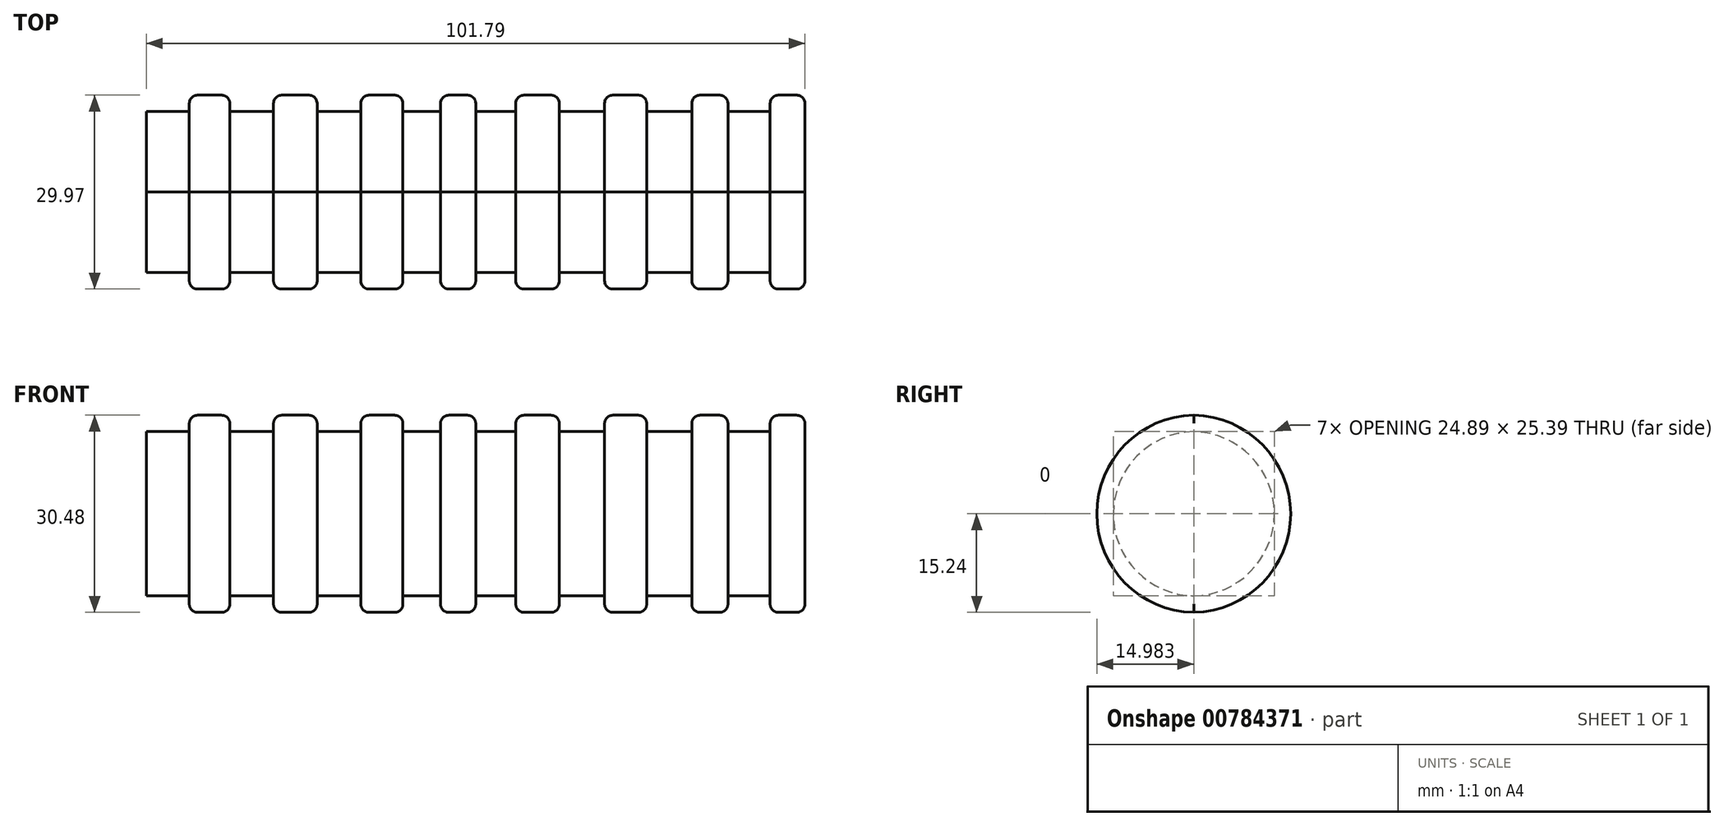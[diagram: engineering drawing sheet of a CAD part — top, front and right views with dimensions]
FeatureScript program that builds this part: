
annotation { "Feature Type Name" : "Feature", "Feature Type Description" : "" }
export const myFeature = defineFeature(function(context is Context, id is Id, definition is map)
    precondition{}
    {
        {
            var Q0;
            Q0=qCreatedBy(makeId("Top.planeOp"),FACE);
            var sketch = newSketch(context, id + "F0", { "sketchPlane" : qUnion([Q0])});
            skLineSegment(sketch, "E0.bottom", {"start": v(-61.73, 35.84) * mm, "end": v(40.06, 35.84) * mm});
            skLineSegment(sketch, "E0.top", {"start": v(-61.73, 10.95) * mm, "end": v(40.06, 10.95) * mm});
            skLineSegment(sketch, "E0.left", {"start": v(-61.73, 35.84) * mm, "end": v(-61.73, 10.95) * mm});
            skLineSegment(sketch, "E0.right", {"start": v(40.06, 35.84) * mm, "end": v(40.06, 10.95) * mm});
            skSolve(sketch);
        }
        {
            var Q0;
            Q0 = qSketchRegion(id + "F0", true);
            extrude(context, id + "F1", {"entities" : qUnion([Q0]), "depth" : 25.4 * mm, "offsetDistance" : 25.4 * mm});
        }
        {
            var Q0;
            Q0=makeQuery(id+"F1.opExtrude","CAP_FACE",FACE,{"disambiguationData":[OSD([sQuery(id+"F0.wireOp",EDGE,"E0.bottom"),sQuery(id+"F0.wireOp",EDGE,"E0.top"),sQuery(id+"F0.wireOp",EDGE,"E0.left"),sQuery(id+"F0.wireOp",EDGE,"E0.right")])],"isStart":false});
            var sketch = newSketch(context, id + "F2", { "sketchPlane" : qUnion([Q0])});
            skLineSegment(sketch, "E1.bottom", {"start": v(-55.11, 35.84) * mm, "end": v(-48.84, 35.84) * mm});
            skLineSegment(sketch, "E1.top", {"start": v(-55.11, 10.95) * mm, "end": v(-48.84, 10.95) * mm});
            skLineSegment(sketch, "E1.left", {"start": v(-55.11, 35.84) * mm, "end": v(-55.11, 10.95) * mm});
            skLineSegment(sketch, "E1.right", {"start": v(-48.84, 35.84) * mm, "end": v(-48.84, 10.95) * mm});
            skLineSegment(sketch, "E2.bottom", {"start": v(-42.09, 35.84) * mm, "end": v(-35.34, 35.84) * mm});
            skLineSegment(sketch, "E2.top", {"start": v(-42.09, 10.95) * mm, "end": v(-35.34, 10.95) * mm});
            skLineSegment(sketch, "E2.left", {"start": v(-42.09, 35.84) * mm, "end": v(-42.09, 10.95) * mm});
            skLineSegment(sketch, "E2.right", {"start": v(-35.34, 35.84) * mm, "end": v(-35.34, 10.95) * mm});
            skLineSegment(sketch, "E3.bottom", {"start": v(-28.6, 35.84) * mm, "end": v(-22.1, 35.84) * mm});
            skLineSegment(sketch, "E3.top", {"start": v(-28.6, 10.95) * mm, "end": v(-22.1, 10.95) * mm});
            skLineSegment(sketch, "E3.left", {"start": v(-28.6, 35.84) * mm, "end": v(-28.6, 10.95) * mm});
            skLineSegment(sketch, "E3.right", {"start": v(-22.1, 35.84) * mm, "end": v(-22.1, 10.95) * mm});
            skLineSegment(sketch, "E4.bottom", {"start": v(-16.27, 35.84) * mm, "end": v(-10.83, 35.84) * mm});
            skLineSegment(sketch, "E4.top", {"start": v(-16.27, 10.95) * mm, "end": v(-10.83, 10.95) * mm});
            skLineSegment(sketch, "E4.left", {"start": v(-16.27, 35.84) * mm, "end": v(-16.27, 10.95) * mm});
            skLineSegment(sketch, "E4.right", {"start": v(-10.83, 35.84) * mm, "end": v(-10.83, 10.95) * mm});
            skLineSegment(sketch, "E5.bottom", {"start": v(-4.64, 35.84) * mm, "end": v(2.1, 35.84) * mm});
            skLineSegment(sketch, "E5.top", {"start": v(-4.64, 10.95) * mm, "end": v(2.1, 10.95) * mm});
            skLineSegment(sketch, "E5.left", {"start": v(-4.64, 35.84) * mm, "end": v(-4.64, 10.95) * mm});
            skLineSegment(sketch, "E5.right", {"start": v(2.1, 35.84) * mm, "end": v(2.1, 10.95) * mm});
            skLineSegment(sketch, "E6.bottom", {"start": v(9.09, 35.84) * mm, "end": v(15.6, 35.84) * mm});
            skLineSegment(sketch, "E6.top", {"start": v(9.09, 10.95) * mm, "end": v(15.6, 10.95) * mm});
            skLineSegment(sketch, "E6.left", {"start": v(9.09, 35.84) * mm, "end": v(9.09, 10.95) * mm});
            skLineSegment(sketch, "E6.right", {"start": v(15.6, 35.84) * mm, "end": v(15.6, 10.95) * mm});
            skLineSegment(sketch, "E7.bottom", {"start": v(22.57, 35.84) * mm, "end": v(28.15, 35.84) * mm});
            skLineSegment(sketch, "E7.top", {"start": v(22.57, 10.95) * mm, "end": v(28.15, 10.95) * mm});
            skLineSegment(sketch, "E7.left", {"start": v(22.57, 35.84) * mm, "end": v(22.57, 10.95) * mm});
            skLineSegment(sketch, "E7.right", {"start": v(28.15, 35.84) * mm, "end": v(28.15, 10.95) * mm});
            skLineSegment(sketch, "E8.bottom", {"start": v(34.68, 35.84) * mm, "end": v(40.06, 35.84) * mm});
            skLineSegment(sketch, "E8.top", {"start": v(34.68, 10.95) * mm, "end": v(40.06, 10.95) * mm});
            skLineSegment(sketch, "E8.left", {"start": v(34.68, 35.84) * mm, "end": v(34.68, 10.95) * mm});
            skLineSegment(sketch, "E8.right", {"start": v(40.06, 35.84) * mm, "end": v(40.06, 10.95) * mm});
            skSolve(sketch);
        }
        {
            var Q0;
            Q0=makeQuery(id+"F2.imprint","IMPRINT",FACE,{"disambiguationData":[TD([[makeQuery(id+"F2.imprint","IMPRINT",EDGE,{"derivedFrom":sQuery(id+"F2.wireOp",EDGE,"E1.bottom")}),-1.0]])]});
            var Q1;
            Q1=makeQuery(id+"F2.imprint","IMPRINT",FACE,{"disambiguationData":[TD([[makeQuery(id+"F2.imprint","IMPRINT",EDGE,{"derivedFrom":sQuery(id+"F2.wireOp",EDGE,"E2.bottom")}),-1.0]])]});
            var Q2;
            Q2=makeQuery(id+"F2.imprint","IMPRINT",FACE,{"disambiguationData":[TD([[makeQuery(id+"F2.imprint","IMPRINT",EDGE,{"derivedFrom":sQuery(id+"F2.wireOp",EDGE,"E3.bottom")}),-1.0]])]});
            var Q3;
            Q3=makeQuery(id+"F2.imprint","IMPRINT",FACE,{"disambiguationData":[TD([[makeQuery(id+"F2.imprint","IMPRINT",EDGE,{"derivedFrom":sQuery(id+"F2.wireOp",EDGE,"E4.bottom")}),-1.0]])]});
            var Q4;
            Q4=makeQuery(id+"F2.imprint","IMPRINT",FACE,{"disambiguationData":[TD([[makeQuery(id+"F2.imprint","IMPRINT",EDGE,{"derivedFrom":sQuery(id+"F2.wireOp",EDGE,"E5.bottom")}),-1.0]])]});
            var Q5;
            Q5=makeQuery(id+"F2.imprint","IMPRINT",FACE,{"disambiguationData":[TD([[makeQuery(id+"F2.imprint","IMPRINT",EDGE,{"derivedFrom":sQuery(id+"F2.wireOp",EDGE,"E6.bottom")}),-1.0]])]});
            var Q6;
            Q6=makeQuery(id+"F2.imprint","IMPRINT",FACE,{"disambiguationData":[TD([[makeQuery(id+"F2.imprint","IMPRINT",EDGE,{"derivedFrom":sQuery(id+"F2.wireOp",EDGE,"E7.bottom")}),-1.0]])]});
            var Q7;
            Q7=makeQuery(id+"F2.imprint","IMPRINT",FACE,{"disambiguationData":[TD([[makeQuery(id+"F2.imprint","IMPRINT",EDGE,{"derivedFrom":sQuery(id+"F2.wireOp",EDGE,"E8.bottom")}),-1.0]])]});
            extrude(context, id + "F3", {"entities" : qUnion([Q0, Q1, Q2, Q3, Q4, Q5, Q6, Q7]), "operationType" : NewBodyOperationType.ADD, "depth" : 2.54 * mm, "offsetDistance" : 25.4 * mm});
        }
        {
            var Q0;
            Q0=makeQuery(id+"F3.boolean.opBoolean","MERGE",FACE,{"derivedFrom":[makeQuery(id+"F1.opExtrude","SWEPT_FACE",FACE,{"disambiguationData":[OSD([sQuery(id+"F0.wireOp",EDGE,"E0.top")])]}),makeQuery(id+"F3.opExtrude","SWEPT_FACE",FACE,{"disambiguationData":[OSD([sQuery(id+"F2.wireOp",EDGE,"E1.top")])]}),makeQuery(id+"F3.opExtrude","SWEPT_FACE",FACE,{"disambiguationData":[OSD([sQuery(id+"F2.wireOp",EDGE,"E2.top")])]}),makeQuery(id+"F3.opExtrude","SWEPT_FACE",FACE,{"disambiguationData":[OSD([sQuery(id+"F2.wireOp",EDGE,"E3.top")])]}),makeQuery(id+"F3.opExtrude","SWEPT_FACE",FACE,{"disambiguationData":[OSD([sQuery(id+"F2.wireOp",EDGE,"E4.top")])]}),makeQuery(id+"F3.opExtrude","SWEPT_FACE",FACE,{"disambiguationData":[OSD([sQuery(id+"F2.wireOp",EDGE,"E5.top")])]}),makeQuery(id+"F3.opExtrude","SWEPT_FACE",FACE,{"disambiguationData":[OSD([sQuery(id+"F2.wireOp",EDGE,"E6.top")])]}),makeQuery(id+"F3.opExtrude","SWEPT_FACE",FACE,{"disambiguationData":[OSD([sQuery(id+"F2.wireOp",EDGE,"E7.top")])]}),makeQuery(id+"F3.opExtrude","SWEPT_FACE",FACE,{"disambiguationData":[OSD([sQuery(id+"F2.wireOp",EDGE,"E8.top")])]})]});
            var sketch = newSketch(context, id + "F4", { "sketchPlane" : qUnion([Q0])});
            skLineSegment(sketch, "E9.bottom", {"start": v(-55.11, 27.94) * mm, "end": v(-48.84, 27.94) * mm});
            skLineSegment(sketch, "E9.top", {"start": v(-55.11, 0) * mm, "end": v(-48.84, 0) * mm});
            skLineSegment(sketch, "E9.left", {"start": v(-55.11, 27.94) * mm, "end": v(-55.11, 0) * mm});
            skLineSegment(sketch, "E9.right", {"start": v(-48.84, 27.94) * mm, "end": v(-48.84, 0) * mm});
            skLineSegment(sketch, "E10.bottom", {"start": v(-42.09, 27.94) * mm, "end": v(-35.34, 27.94) * mm});
            skLineSegment(sketch, "E10.top", {"start": v(-42.09, 0) * mm, "end": v(-35.34, 0) * mm});
            skLineSegment(sketch, "E10.left", {"start": v(-42.09, 27.94) * mm, "end": v(-42.09, 0) * mm});
            skLineSegment(sketch, "E10.right", {"start": v(-35.34, 27.94) * mm, "end": v(-35.34, 0) * mm});
            skLineSegment(sketch, "E11.bottom", {"start": v(-28.6, 27.94) * mm, "end": v(-22.1, 27.94) * mm});
            skLineSegment(sketch, "E11.top", {"start": v(-28.6, 0) * mm, "end": v(-22.1, 0) * mm});
            skLineSegment(sketch, "E11.left", {"start": v(-28.6, 27.94) * mm, "end": v(-28.6, 0) * mm});
            skLineSegment(sketch, "E11.right", {"start": v(-22.1, 27.94) * mm, "end": v(-22.1, 0) * mm});
            skLineSegment(sketch, "E12.bottom", {"start": v(-16.27, 27.94) * mm, "end": v(-10.83, 27.94) * mm});
            skLineSegment(sketch, "E12.top", {"start": v(-16.27, 0) * mm, "end": v(-10.83, 0) * mm});
            skLineSegment(sketch, "E12.left", {"start": v(-16.27, 27.94) * mm, "end": v(-16.27, 0) * mm});
            skLineSegment(sketch, "E12.right", {"start": v(-10.83, 27.94) * mm, "end": v(-10.83, 0) * mm});
            skLineSegment(sketch, "E13.bottom", {"start": v(-4.64, 27.94) * mm, "end": v(2.1, 27.94) * mm});
            skLineSegment(sketch, "E13.top", {"start": v(-4.64, 0) * mm, "end": v(2.1, 0) * mm});
            skLineSegment(sketch, "E13.left", {"start": v(-4.64, 27.94) * mm, "end": v(-4.64, 0) * mm});
            skLineSegment(sketch, "E13.right", {"start": v(2.1, 27.94) * mm, "end": v(2.1, 0) * mm});
            skLineSegment(sketch, "E14.bottom", {"start": v(9.09, 27.94) * mm, "end": v(15.6, 27.94) * mm});
            skLineSegment(sketch, "E14.top", {"start": v(9.09, 0) * mm, "end": v(15.6, 0) * mm});
            skLineSegment(sketch, "E14.left", {"start": v(9.09, 27.94) * mm, "end": v(9.09, 0) * mm});
            skLineSegment(sketch, "E14.right", {"start": v(15.6, 27.94) * mm, "end": v(15.6, 0) * mm});
            skLineSegment(sketch, "E15.bottom", {"start": v(22.57, 27.94) * mm, "end": v(28.15, 27.94) * mm});
            skLineSegment(sketch, "E15.top", {"start": v(22.57, 0) * mm, "end": v(28.15, 0) * mm});
            skLineSegment(sketch, "E15.left", {"start": v(22.57, 27.94) * mm, "end": v(22.57, 0) * mm});
            skLineSegment(sketch, "E15.right", {"start": v(28.15, 27.94) * mm, "end": v(28.15, 0) * mm});
            skLineSegment(sketch, "E16.bottom", {"start": v(34.68, 27.94) * mm, "end": v(40.06, 27.94) * mm});
            skLineSegment(sketch, "E16.top", {"start": v(34.68, 0) * mm, "end": v(40.06, 0) * mm});
            skLineSegment(sketch, "E16.left", {"start": v(34.68, 27.94) * mm, "end": v(34.68, 0) * mm});
            skLineSegment(sketch, "E16.right", {"start": v(40.06, 27.94) * mm, "end": v(40.06, 0) * mm});
            skSolve(sketch);
        }
        {
            var Q0;
            {var subQ1=sQuery(id+"F4.wireOp",EDGE,"E9.bottom");Q0=makeQuery(id+"F4.imprint","IMPRINT",FACE,{"disambiguationData":[TD([[makeQuery(id+"F4.imprint","IMPRINT",EDGE,{"derivedFrom":subQ1}),-1.0]])]});}
            var Q1;
            {var subQ1=sQuery(id+"F4.wireOp",EDGE,"E10.bottom");Q1=makeQuery(id+"F4.imprint","IMPRINT",FACE,{"disambiguationData":[TD([[makeQuery(id+"F4.imprint","IMPRINT",EDGE,{"derivedFrom":subQ1}),-1.0]])]});}
            var Q2;
            {var subQ1=sQuery(id+"F4.wireOp",EDGE,"E11.bottom");Q2=makeQuery(id+"F4.imprint","IMPRINT",FACE,{"disambiguationData":[TD([[makeQuery(id+"F4.imprint","IMPRINT",EDGE,{"derivedFrom":subQ1}),-1.0]])]});}
            var Q3;
            {var subQ1=sQuery(id+"F4.wireOp",EDGE,"E12.bottom");Q3=makeQuery(id+"F4.imprint","IMPRINT",FACE,{"disambiguationData":[TD([[makeQuery(id+"F4.imprint","IMPRINT",EDGE,{"derivedFrom":subQ1}),-1.0]])]});}
            var Q4;
            {var subQ1=sQuery(id+"F4.wireOp",EDGE,"E13.bottom");Q4=makeQuery(id+"F4.imprint","IMPRINT",FACE,{"disambiguationData":[TD([[makeQuery(id+"F4.imprint","IMPRINT",EDGE,{"derivedFrom":subQ1}),-1.0]])]});}
            var Q5;
            {var subQ1=sQuery(id+"F4.wireOp",EDGE,"E14.bottom");Q5=makeQuery(id+"F4.imprint","IMPRINT",FACE,{"disambiguationData":[TD([[makeQuery(id+"F4.imprint","IMPRINT",EDGE,{"derivedFrom":subQ1}),-1.0]])]});}
            var Q6;
            {var subQ1=sQuery(id+"F4.wireOp",EDGE,"E15.bottom");Q6=makeQuery(id+"F4.imprint","IMPRINT",FACE,{"disambiguationData":[TD([[makeQuery(id+"F4.imprint","IMPRINT",EDGE,{"derivedFrom":subQ1}),-1.0]])]});}
            var Q7;
            {var subQ1=sQuery(id+"F4.wireOp",EDGE,"E16.bottom");Q7=makeQuery(id+"F4.imprint","IMPRINT",FACE,{"disambiguationData":[TD([[makeQuery(id+"F4.imprint","IMPRINT",EDGE,{"derivedFrom":subQ1}),-1.0]])]});}
            extrude(context, id + "F5", {"entities" : qUnion([Q0, Q1, Q2, Q3, Q4, Q5, Q6, Q7]), "operationType" : NewBodyOperationType.ADD, "depth" : 2.54 * mm, "offsetDistance" : 25.4 * mm});
        }
        {
            var Q0;
            Q0=makeQuery(id+"F5.boolean.opBoolean","MERGE",FACE,{"derivedFrom":[makeQuery(id+"F1.opExtrude","CAP_FACE",FACE,{"disambiguationData":[OSD([sQuery(id+"F0.wireOp",EDGE,"E0.bottom"),sQuery(id+"F0.wireOp",EDGE,"E0.top"),sQuery(id+"F0.wireOp",EDGE,"E0.left"),sQuery(id+"F0.wireOp",EDGE,"E0.right")])],"isStart":true}),makeQuery(id+"F5.opExtrude","SWEPT_FACE",FACE,{"disambiguationData":[OSD([sQuery(id+"F4.wireOp",EDGE,"E9.top")])]}),makeQuery(id+"F5.opExtrude","SWEPT_FACE",FACE,{"disambiguationData":[OSD([sQuery(id+"F4.wireOp",EDGE,"E10.top")])]}),makeQuery(id+"F5.opExtrude","SWEPT_FACE",FACE,{"disambiguationData":[OSD([sQuery(id+"F4.wireOp",EDGE,"E11.top")])]}),makeQuery(id+"F5.opExtrude","SWEPT_FACE",FACE,{"disambiguationData":[OSD([sQuery(id+"F4.wireOp",EDGE,"E12.top")])]}),makeQuery(id+"F5.opExtrude","SWEPT_FACE",FACE,{"disambiguationData":[OSD([sQuery(id+"F4.wireOp",EDGE,"E13.top")])]}),makeQuery(id+"F5.opExtrude","SWEPT_FACE",FACE,{"disambiguationData":[OSD([sQuery(id+"F4.wireOp",EDGE,"E14.top")])]}),makeQuery(id+"F5.opExtrude","SWEPT_FACE",FACE,{"disambiguationData":[OSD([sQuery(id+"F4.wireOp",EDGE,"E15.top")])]}),makeQuery(id+"F5.opExtrude","SWEPT_FACE",FACE,{"disambiguationData":[OSD([sQuery(id+"F4.wireOp",EDGE,"E16.top")])]})]});
            var sketch = newSketch(context, id + "F6", { "sketchPlane" : qUnion([Q0])});
            skLineSegment(sketch, "E17.bottom", {"start": v(-55.11, -8.4) * mm, "end": v(-48.84, -8.4) * mm});
            skLineSegment(sketch, "E17.top", {"start": v(-55.11, -35.84) * mm, "end": v(-48.84, -35.84) * mm});
            skLineSegment(sketch, "E17.left", {"start": v(-55.11, -8.4) * mm, "end": v(-55.11, -35.84) * mm});
            skLineSegment(sketch, "E17.right", {"start": v(-48.84, -8.4) * mm, "end": v(-48.84, -35.84) * mm});
            skLineSegment(sketch, "E18.bottom", {"start": v(-42.09, -8.4) * mm, "end": v(-35.34, -8.4) * mm});
            skLineSegment(sketch, "E18.top", {"start": v(-42.09, -35.84) * mm, "end": v(-35.34, -35.84) * mm});
            skLineSegment(sketch, "E18.left", {"start": v(-42.09, -8.4) * mm, "end": v(-42.09, -35.84) * mm});
            skLineSegment(sketch, "E18.right", {"start": v(-35.34, -8.4) * mm, "end": v(-35.34, -35.84) * mm});
            skLineSegment(sketch, "E19.bottom", {"start": v(-28.6, -8.4) * mm, "end": v(-22.1, -8.4) * mm});
            skLineSegment(sketch, "E19.top", {"start": v(-28.6, -35.84) * mm, "end": v(-22.1, -35.84) * mm});
            skLineSegment(sketch, "E19.left", {"start": v(-28.6, -8.4) * mm, "end": v(-28.6, -35.84) * mm});
            skLineSegment(sketch, "E19.right", {"start": v(-22.1, -8.4) * mm, "end": v(-22.1, -35.84) * mm});
            skLineSegment(sketch, "E20.bottom", {"start": v(-16.27, -8.4) * mm, "end": v(-10.83, -8.4) * mm});
            skLineSegment(sketch, "E20.top", {"start": v(-16.27, -35.84) * mm, "end": v(-10.83, -35.84) * mm});
            skLineSegment(sketch, "E20.left", {"start": v(-16.27, -8.4) * mm, "end": v(-16.27, -35.84) * mm});
            skLineSegment(sketch, "E20.right", {"start": v(-10.83, -8.4) * mm, "end": v(-10.83, -35.84) * mm});
            skLineSegment(sketch, "E21.bottom", {"start": v(-4.64, -8.4) * mm, "end": v(2.1, -8.4) * mm});
            skLineSegment(sketch, "E21.top", {"start": v(-4.64, -35.84) * mm, "end": v(2.1, -35.84) * mm});
            skLineSegment(sketch, "E21.left", {"start": v(-4.64, -8.4) * mm, "end": v(-4.64, -35.84) * mm});
            skLineSegment(sketch, "E21.right", {"start": v(2.1, -8.4) * mm, "end": v(2.1, -35.84) * mm});
            skLineSegment(sketch, "E22.bottom", {"start": v(9.09, -8.4) * mm, "end": v(15.6, -8.4) * mm});
            skLineSegment(sketch, "E22.top", {"start": v(9.09, -35.84) * mm, "end": v(15.6, -35.84) * mm});
            skLineSegment(sketch, "E22.left", {"start": v(9.09, -8.4) * mm, "end": v(9.09, -35.84) * mm});
            skLineSegment(sketch, "E22.right", {"start": v(15.6, -8.4) * mm, "end": v(15.6, -35.84) * mm});
            skLineSegment(sketch, "E23.bottom", {"start": v(22.57, -8.4) * mm, "end": v(28.15, -8.4) * mm});
            skLineSegment(sketch, "E23.top", {"start": v(22.57, -35.84) * mm, "end": v(28.15, -35.84) * mm});
            skLineSegment(sketch, "E23.left", {"start": v(22.57, -8.4) * mm, "end": v(22.57, -35.84) * mm});
            skLineSegment(sketch, "E23.right", {"start": v(28.15, -8.4) * mm, "end": v(28.15, -35.84) * mm});
            skLineSegment(sketch, "E24.bottom", {"start": v(34.68, -8.4) * mm, "end": v(40.06, -8.4) * mm});
            skLineSegment(sketch, "E24.top", {"start": v(34.68, -35.84) * mm, "end": v(40.06, -35.84) * mm});
            skLineSegment(sketch, "E24.left", {"start": v(34.68, -8.4) * mm, "end": v(34.68, -35.84) * mm});
            skLineSegment(sketch, "E24.right", {"start": v(40.06, -8.4) * mm, "end": v(40.06, -35.84) * mm});
            skSolve(sketch);
        }
        {
            var Q0;
            {var subQ1=sQuery(id+"F6.wireOp",EDGE,"E17.bottom");Q0=makeQuery(id+"F6.imprint","IMPRINT",FACE,{"disambiguationData":[TD([[makeQuery(id+"F6.imprint","IMPRINT",EDGE,{"derivedFrom":subQ1}),-1.0]])]});}
            var Q1;
            {var subQ1=sQuery(id+"F6.wireOp",EDGE,"E18.bottom");Q1=makeQuery(id+"F6.imprint","IMPRINT",FACE,{"disambiguationData":[TD([[makeQuery(id+"F6.imprint","IMPRINT",EDGE,{"derivedFrom":subQ1}),-1.0]])]});}
            var Q2;
            {var subQ1=sQuery(id+"F6.wireOp",EDGE,"E19.bottom");Q2=makeQuery(id+"F6.imprint","IMPRINT",FACE,{"disambiguationData":[TD([[makeQuery(id+"F6.imprint","IMPRINT",EDGE,{"derivedFrom":subQ1}),-1.0]])]});}
            var Q3;
            {var subQ1=sQuery(id+"F6.wireOp",EDGE,"E20.bottom");Q3=makeQuery(id+"F6.imprint","IMPRINT",FACE,{"disambiguationData":[TD([[makeQuery(id+"F6.imprint","IMPRINT",EDGE,{"derivedFrom":subQ1}),-1.0]])]});}
            var Q4;
            {var subQ1=sQuery(id+"F6.wireOp",EDGE,"E21.bottom");Q4=makeQuery(id+"F6.imprint","IMPRINT",FACE,{"disambiguationData":[TD([[makeQuery(id+"F6.imprint","IMPRINT",EDGE,{"derivedFrom":subQ1}),-1.0]])]});}
            var Q5;
            {var subQ1=sQuery(id+"F6.wireOp",EDGE,"E22.bottom");Q5=makeQuery(id+"F6.imprint","IMPRINT",FACE,{"disambiguationData":[TD([[makeQuery(id+"F6.imprint","IMPRINT",EDGE,{"derivedFrom":subQ1}),-1.0]])]});}
            var Q6;
            {var subQ1=sQuery(id+"F6.wireOp",EDGE,"E23.bottom");Q6=makeQuery(id+"F6.imprint","IMPRINT",FACE,{"disambiguationData":[TD([[makeQuery(id+"F6.imprint","IMPRINT",EDGE,{"derivedFrom":subQ1}),-1.0]])]});}
            var Q7;
            {var subQ1=sQuery(id+"F6.wireOp",EDGE,"E24.bottom");Q7=makeQuery(id+"F6.imprint","IMPRINT",FACE,{"disambiguationData":[TD([[makeQuery(id+"F6.imprint","IMPRINT",EDGE,{"derivedFrom":subQ1}),-1.0]])]});}
            extrude(context, id + "F7", {"entities" : qUnion([Q0, Q1, Q2, Q3, Q4, Q5, Q6, Q7]), "operationType" : NewBodyOperationType.ADD, "depth" : 2.54 * mm, "offsetDistance" : 25.4 * mm});
        }
        {
            var Q0;
            Q0=makeQuery(id+"F7.boolean.opBoolean","MERGE",FACE,{"derivedFrom":[makeQuery(id+"F3.boolean.opBoolean","MERGE",FACE,{"derivedFrom":[makeQuery(id+"F1.opExtrude","SWEPT_FACE",FACE,{"disambiguationData":[OSD([sQuery(id+"F0.wireOp",EDGE,"E0.bottom")])]}),makeQuery(id+"F3.opExtrude","SWEPT_FACE",FACE,{"disambiguationData":[OSD([sQuery(id+"F2.wireOp",EDGE,"E1.bottom")])]}),makeQuery(id+"F3.opExtrude","SWEPT_FACE",FACE,{"disambiguationData":[OSD([sQuery(id+"F2.wireOp",EDGE,"E2.bottom")])]}),makeQuery(id+"F3.opExtrude","SWEPT_FACE",FACE,{"disambiguationData":[OSD([sQuery(id+"F2.wireOp",EDGE,"E3.bottom")])]}),makeQuery(id+"F3.opExtrude","SWEPT_FACE",FACE,{"disambiguationData":[OSD([sQuery(id+"F2.wireOp",EDGE,"E4.bottom")])]}),makeQuery(id+"F3.opExtrude","SWEPT_FACE",FACE,{"disambiguationData":[OSD([sQuery(id+"F2.wireOp",EDGE,"E5.bottom")])]}),makeQuery(id+"F3.opExtrude","SWEPT_FACE",FACE,{"disambiguationData":[OSD([sQuery(id+"F2.wireOp",EDGE,"E6.bottom")])]}),makeQuery(id+"F3.opExtrude","SWEPT_FACE",FACE,{"disambiguationData":[OSD([sQuery(id+"F2.wireOp",EDGE,"E7.bottom")])]}),makeQuery(id+"F3.opExtrude","SWEPT_FACE",FACE,{"disambiguationData":[OSD([sQuery(id+"F2.wireOp",EDGE,"E8.bottom")])]})]}),makeQuery(id+"F7.opExtrude","SWEPT_FACE",FACE,{"disambiguationData":[OSD([sQuery(id+"F6.wireOp",EDGE,"E17.top")])]}),makeQuery(id+"F7.opExtrude","SWEPT_FACE",FACE,{"disambiguationData":[OSD([sQuery(id+"F6.wireOp",EDGE,"E18.top")])]}),makeQuery(id+"F7.opExtrude","SWEPT_FACE",FACE,{"disambiguationData":[OSD([sQuery(id+"F6.wireOp",EDGE,"E19.top")])]}),makeQuery(id+"F7.opExtrude","SWEPT_FACE",FACE,{"disambiguationData":[OSD([sQuery(id+"F6.wireOp",EDGE,"E20.top")])]}),makeQuery(id+"F7.opExtrude","SWEPT_FACE",FACE,{"disambiguationData":[OSD([sQuery(id+"F6.wireOp",EDGE,"E21.top")])]}),makeQuery(id+"F7.opExtrude","SWEPT_FACE",FACE,{"disambiguationData":[OSD([sQuery(id+"F6.wireOp",EDGE,"E22.top")])]}),makeQuery(id+"F7.opExtrude","SWEPT_FACE",FACE,{"disambiguationData":[OSD([sQuery(id+"F6.wireOp",EDGE,"E23.top")])]}),makeQuery(id+"F7.opExtrude","SWEPT_FACE",FACE,{"disambiguationData":[OSD([sQuery(id+"F6.wireOp",EDGE,"E24.top")])]})]});
            var sketch = newSketch(context, id + "F8", { "sketchPlane" : qUnion([Q0])});
            skLineSegment(sketch, "E25.bottom", {"start": v(-40.06, 27.94) * mm, "end": v(-34.68, 27.94) * mm});
            skLineSegment(sketch, "E25.top", {"start": v(-40.06, -2.54) * mm, "end": v(-34.68, -2.54) * mm});
            skLineSegment(sketch, "E25.left", {"start": v(-40.06, 27.94) * mm, "end": v(-40.06, -2.54) * mm});
            skLineSegment(sketch, "E25.right", {"start": v(-34.68, 27.94) * mm, "end": v(-34.68, -2.54) * mm});
            skLineSegment(sketch, "E26.bottom", {"start": v(-28.15, 27.94) * mm, "end": v(-22.57, 27.94) * mm});
            skLineSegment(sketch, "E26.top", {"start": v(-28.15, -2.54) * mm, "end": v(-22.57, -2.54) * mm});
            skLineSegment(sketch, "E26.left", {"start": v(-28.15, 27.94) * mm, "end": v(-28.15, -2.54) * mm});
            skLineSegment(sketch, "E26.right", {"start": v(-22.57, 27.94) * mm, "end": v(-22.57, -2.54) * mm});
            skLineSegment(sketch, "E27.bottom", {"start": v(-15.6, 27.94) * mm, "end": v(-9.09, 27.94) * mm});
            skLineSegment(sketch, "E27.top", {"start": v(-15.6, -2.54) * mm, "end": v(-9.09, -2.54) * mm});
            skLineSegment(sketch, "E27.left", {"start": v(-15.6, 27.94) * mm, "end": v(-15.6, -2.54) * mm});
            skLineSegment(sketch, "E27.right", {"start": v(-9.09, 27.94) * mm, "end": v(-9.09, -2.54) * mm});
            skLineSegment(sketch, "E28.bottom", {"start": v(-2.1, 27.94) * mm, "end": v(4.64, 27.94) * mm});
            skLineSegment(sketch, "E28.top", {"start": v(-2.1, -2.54) * mm, "end": v(4.64, -2.54) * mm});
            skLineSegment(sketch, "E28.left", {"start": v(-2.1, 27.94) * mm, "end": v(-2.1, -2.54) * mm});
            skLineSegment(sketch, "E28.right", {"start": v(4.64, 27.94) * mm, "end": v(4.64, -2.54) * mm});
            skLineSegment(sketch, "E29.bottom", {"start": v(10.83, 27.94) * mm, "end": v(16.27, 27.94) * mm});
            skLineSegment(sketch, "E29.top", {"start": v(10.83, -2.54) * mm, "end": v(16.27, -2.54) * mm});
            skLineSegment(sketch, "E29.left", {"start": v(10.83, 27.94) * mm, "end": v(10.83, -2.54) * mm});
            skLineSegment(sketch, "E29.right", {"start": v(16.27, 27.94) * mm, "end": v(16.27, -2.54) * mm});
            skLineSegment(sketch, "E30.bottom", {"start": v(22.1, 27.94) * mm, "end": v(28.6, 27.94) * mm});
            skLineSegment(sketch, "E30.top", {"start": v(22.1, -2.54) * mm, "end": v(28.6, -2.54) * mm});
            skLineSegment(sketch, "E30.left", {"start": v(22.1, 27.94) * mm, "end": v(22.1, -2.54) * mm});
            skLineSegment(sketch, "E30.right", {"start": v(28.6, 27.94) * mm, "end": v(28.6, -2.54) * mm});
            skLineSegment(sketch, "E31.bottom", {"start": v(35.34, 27.94) * mm, "end": v(42.09, 27.94) * mm});
            skLineSegment(sketch, "E31.top", {"start": v(35.34, -2.54) * mm, "end": v(42.09, -2.54) * mm});
            skLineSegment(sketch, "E31.left", {"start": v(35.34, 27.94) * mm, "end": v(35.34, -2.54) * mm});
            skLineSegment(sketch, "E31.right", {"start": v(42.09, 27.94) * mm, "end": v(42.09, -2.54) * mm});
            skLineSegment(sketch, "E32.bottom", {"start": v(48.84, 27.94) * mm, "end": v(55.11, 27.94) * mm});
            skLineSegment(sketch, "E32.top", {"start": v(48.84, -2.54) * mm, "end": v(55.11, -2.54) * mm});
            skLineSegment(sketch, "E32.left", {"start": v(48.84, 27.94) * mm, "end": v(48.84, -2.54) * mm});
            skLineSegment(sketch, "E32.right", {"start": v(55.11, 27.94) * mm, "end": v(55.11, -2.54) * mm});
            skSolve(sketch);
        }
        {
            var Q0;
            {var subQ19=sQuery(id+"F8.wireOp",EDGE,"E25.bottom");Q0=makeQuery(id+"F8.imprint","IMPRINT",FACE,{"disambiguationData":[TD([[makeQuery(id+"F8.imprint","IMPRINT",EDGE,{"derivedFrom":subQ19}),1.0]])]});}
            var Q1;
            {var subQ1=sQuery(id+"F8.wireOp",EDGE,"E26.bottom");Q1=makeQuery(id+"F8.imprint","IMPRINT",FACE,{"disambiguationData":[TD([[makeQuery(id+"F8.imprint","IMPRINT",EDGE,{"derivedFrom":subQ1}),1.0]])]});}
            var Q2;
            {var subQ39=sQuery(id+"F8.wireOp",EDGE,"E27.bottom");Q2=makeQuery(id+"F8.imprint","IMPRINT",FACE,{"disambiguationData":[TD([[makeQuery(id+"F8.imprint","IMPRINT",EDGE,{"derivedFrom":subQ39}),1.0]])]});}
            var Q3;
            {var subQ39=sQuery(id+"F8.wireOp",EDGE,"E28.bottom");Q3=makeQuery(id+"F8.imprint","IMPRINT",FACE,{"disambiguationData":[TD([[makeQuery(id+"F8.imprint","IMPRINT",EDGE,{"derivedFrom":subQ39}),1.0]])]});}
            var Q4;
            {var subQ39=sQuery(id+"F8.wireOp",EDGE,"E29.bottom");Q4=makeQuery(id+"F8.imprint","IMPRINT",FACE,{"disambiguationData":[TD([[makeQuery(id+"F8.imprint","IMPRINT",EDGE,{"derivedFrom":subQ39}),1.0]])]});}
            var Q5;
            {var subQ39=sQuery(id+"F8.wireOp",EDGE,"E30.bottom");Q5=makeQuery(id+"F8.imprint","IMPRINT",FACE,{"disambiguationData":[TD([[makeQuery(id+"F8.imprint","IMPRINT",EDGE,{"derivedFrom":subQ39}),1.0]])]});}
            var Q6;
            {var subQ39=sQuery(id+"F8.wireOp",EDGE,"E31.bottom");Q6=makeQuery(id+"F8.imprint","IMPRINT",FACE,{"disambiguationData":[TD([[makeQuery(id+"F8.imprint","IMPRINT",EDGE,{"derivedFrom":subQ39}),1.0]])]});}
            var Q7;
            {var subQ1=sQuery(id+"F8.wireOp",EDGE,"E32.bottom");Q7=makeQuery(id+"F8.imprint","IMPRINT",FACE,{"disambiguationData":[TD([[makeQuery(id+"F8.imprint","IMPRINT",EDGE,{"derivedFrom":subQ1}),1.0]])]});}
            extrude(context, id + "F9", {"entities" : qUnion([Q0, Q1, Q2, Q3, Q4, Q5, Q6, Q7]), "operationType" : NewBodyOperationType.ADD, "depth" : 2.54 * mm, "offsetDistance" : 25.4 * mm});
        }
        {
            var Q0;
            {var subQ0=sQuery(id+"F0.wireOp",EDGE,"E0.bottom");Q0=makeQuery(id+"F7.boolean.opBoolean","SPLIT",EDGE,{"disambiguationData":[TD([makeQuery(id+"F3.opExtrude","SWEPT_FACE",FACE,{"disambiguationData":[OSD([sQuery(id+"F2.wireOp",EDGE,"E7.right")])]})])],"derivedFrom":makeQuery(id+"F1.opExtrude","CAP_EDGE",EDGE,{"disambiguationData":[OSD([subQ0])],"isStart":true})});}
            var Q1;
            {var subQ0=sQuery(id+"F0.wireOp",EDGE,"E0.bottom");Q1=makeQuery(id+"F7.boolean.opBoolean","SPLIT",EDGE,{"disambiguationData":[TD([makeQuery(id+"F3.opExtrude","SWEPT_FACE",FACE,{"disambiguationData":[OSD([sQuery(id+"F2.wireOp",EDGE,"E6.right")])]})])],"derivedFrom":makeQuery(id+"F1.opExtrude","CAP_EDGE",EDGE,{"disambiguationData":[OSD([subQ0])],"isStart":true})});}
            var Q2;
            {var subQ0=sQuery(id+"F0.wireOp",EDGE,"E0.bottom");Q2=makeQuery(id+"F7.boolean.opBoolean","SPLIT",EDGE,{"disambiguationData":[TD([makeQuery(id+"F3.opExtrude","SWEPT_FACE",FACE,{"disambiguationData":[OSD([sQuery(id+"F2.wireOp",EDGE,"E5.right")])]})])],"derivedFrom":makeQuery(id+"F1.opExtrude","CAP_EDGE",EDGE,{"disambiguationData":[OSD([subQ0])],"isStart":true})});}
            var Q3;
            {var subQ0=sQuery(id+"F0.wireOp",EDGE,"E0.bottom");Q3=makeQuery(id+"F7.boolean.opBoolean","SPLIT",EDGE,{"disambiguationData":[TD([makeQuery(id+"F3.opExtrude","SWEPT_FACE",FACE,{"disambiguationData":[OSD([sQuery(id+"F2.wireOp",EDGE,"E4.right")])]})])],"derivedFrom":makeQuery(id+"F1.opExtrude","CAP_EDGE",EDGE,{"disambiguationData":[OSD([subQ0])],"isStart":true})});}
            var Q4;
            {var subQ0=sQuery(id+"F0.wireOp",EDGE,"E0.bottom");Q4=makeQuery(id+"F7.boolean.opBoolean","SPLIT",EDGE,{"disambiguationData":[TD([makeQuery(id+"F3.opExtrude","SWEPT_FACE",FACE,{"disambiguationData":[OSD([sQuery(id+"F2.wireOp",EDGE,"E3.right")])]})])],"derivedFrom":makeQuery(id+"F1.opExtrude","CAP_EDGE",EDGE,{"disambiguationData":[OSD([subQ0])],"isStart":true})});}
            var Q5;
            {var subQ0=sQuery(id+"F0.wireOp",EDGE,"E0.bottom");Q5=makeQuery(id+"F7.boolean.opBoolean","SPLIT",EDGE,{"disambiguationData":[TD([makeQuery(id+"F3.opExtrude","SWEPT_FACE",FACE,{"disambiguationData":[OSD([sQuery(id+"F2.wireOp",EDGE,"E2.right")])]})])],"derivedFrom":makeQuery(id+"F1.opExtrude","CAP_EDGE",EDGE,{"disambiguationData":[OSD([subQ0])],"isStart":true})});}
            var Q6;
            {var subQ0=sQuery(id+"F0.wireOp",EDGE,"E0.bottom");Q6=makeQuery(id+"F7.boolean.opBoolean","SPLIT",EDGE,{"disambiguationData":[TD([makeQuery(id+"F3.opExtrude","SWEPT_FACE",FACE,{"disambiguationData":[OSD([sQuery(id+"F2.wireOp",EDGE,"E1.right")])]})])],"derivedFrom":makeQuery(id+"F1.opExtrude","CAP_EDGE",EDGE,{"disambiguationData":[OSD([subQ0])],"isStart":true})});}
            var Q7;
            {var subQ0=sQuery(id+"F0.wireOp",EDGE,"E0.left");var subQ1=sQuery(id+"F0.wireOp",EDGE,"E0.bottom");Q7=makeQuery(id+"F7.boolean.opBoolean","SPLIT",EDGE,{"disambiguationData":[TD([makeQuery(id+"F1.opExtrude","SWEPT_FACE",FACE,{"disambiguationData":[OSD([subQ0])]})])],"derivedFrom":makeQuery(id+"F1.opExtrude","CAP_EDGE",EDGE,{"disambiguationData":[OSD([subQ1])],"isStart":true})});}
            var Q8;
            {var subQ0=sQuery(id+"F0.wireOp",EDGE,"E0.top");Q8=makeQuery(id+"F5.boolean.opBoolean","SPLIT",EDGE,{"disambiguationData":[TD([makeQuery(id+"F3.opExtrude","SWEPT_FACE",FACE,{"disambiguationData":[OSD([sQuery(id+"F2.wireOp",EDGE,"E7.right")])]})])],"derivedFrom":makeQuery(id+"F1.opExtrude","CAP_EDGE",EDGE,{"disambiguationData":[OSD([subQ0])],"isStart":true})});}
            var Q9;
            {var subQ0=sQuery(id+"F0.wireOp",EDGE,"E0.top");Q9=makeQuery(id+"F5.boolean.opBoolean","SPLIT",EDGE,{"disambiguationData":[TD([makeQuery(id+"F3.opExtrude","SWEPT_FACE",FACE,{"disambiguationData":[OSD([sQuery(id+"F2.wireOp",EDGE,"E6.right")])]})])],"derivedFrom":makeQuery(id+"F1.opExtrude","CAP_EDGE",EDGE,{"disambiguationData":[OSD([subQ0])],"isStart":true})});}
            var Q10;
            {var subQ0=sQuery(id+"F0.wireOp",EDGE,"E0.top");Q10=makeQuery(id+"F5.boolean.opBoolean","SPLIT",EDGE,{"disambiguationData":[TD([makeQuery(id+"F3.opExtrude","SWEPT_FACE",FACE,{"disambiguationData":[OSD([sQuery(id+"F2.wireOp",EDGE,"E5.right")])]})])],"derivedFrom":makeQuery(id+"F1.opExtrude","CAP_EDGE",EDGE,{"disambiguationData":[OSD([subQ0])],"isStart":true})});}
            var Q11;
            {var subQ0=sQuery(id+"F0.wireOp",EDGE,"E0.top");Q11=makeQuery(id+"F5.boolean.opBoolean","SPLIT",EDGE,{"disambiguationData":[TD([makeQuery(id+"F3.opExtrude","SWEPT_FACE",FACE,{"disambiguationData":[OSD([sQuery(id+"F2.wireOp",EDGE,"E4.right")])]})])],"derivedFrom":makeQuery(id+"F1.opExtrude","CAP_EDGE",EDGE,{"disambiguationData":[OSD([subQ0])],"isStart":true})});}
            var Q12;
            {var subQ0=sQuery(id+"F0.wireOp",EDGE,"E0.top");Q12=makeQuery(id+"F5.boolean.opBoolean","SPLIT",EDGE,{"disambiguationData":[TD([makeQuery(id+"F3.opExtrude","SWEPT_FACE",FACE,{"disambiguationData":[OSD([sQuery(id+"F2.wireOp",EDGE,"E3.right")])]})])],"derivedFrom":makeQuery(id+"F1.opExtrude","CAP_EDGE",EDGE,{"disambiguationData":[OSD([subQ0])],"isStart":true})});}
            var Q13;
            {var subQ0=sQuery(id+"F0.wireOp",EDGE,"E0.top");Q13=makeQuery(id+"F5.boolean.opBoolean","SPLIT",EDGE,{"disambiguationData":[TD([makeQuery(id+"F3.opExtrude","SWEPT_FACE",FACE,{"disambiguationData":[OSD([sQuery(id+"F2.wireOp",EDGE,"E2.right")])]})])],"derivedFrom":makeQuery(id+"F1.opExtrude","CAP_EDGE",EDGE,{"disambiguationData":[OSD([subQ0])],"isStart":true})});}
            var Q14;
            {var subQ0=sQuery(id+"F0.wireOp",EDGE,"E0.top");Q14=makeQuery(id+"F5.boolean.opBoolean","SPLIT",EDGE,{"disambiguationData":[TD([makeQuery(id+"F3.opExtrude","SWEPT_FACE",FACE,{"disambiguationData":[OSD([sQuery(id+"F2.wireOp",EDGE,"E1.right")])]})])],"derivedFrom":makeQuery(id+"F1.opExtrude","CAP_EDGE",EDGE,{"disambiguationData":[OSD([subQ0])],"isStart":true})});}
            var Q15;
            {var subQ0=sQuery(id+"F0.wireOp",EDGE,"E0.left");var subQ1=sQuery(id+"F0.wireOp",EDGE,"E0.top");Q15=makeQuery(id+"F5.boolean.opBoolean","SPLIT",EDGE,{"disambiguationData":[TD([makeQuery(id+"F1.opExtrude","SWEPT_FACE",FACE,{"disambiguationData":[OSD([subQ0])]})])],"derivedFrom":makeQuery(id+"F1.opExtrude","CAP_EDGE",EDGE,{"disambiguationData":[OSD([subQ1])],"isStart":true})});}
            var Q16;
            {var subQ0=sQuery(id+"F0.wireOp",EDGE,"E0.top");Q16=makeQuery(id+"F3.boolean.opBoolean","SPLIT",EDGE,{"disambiguationData":[TD([makeQuery(id+"F3.opExtrude","SWEPT_FACE",FACE,{"disambiguationData":[OSD([sQuery(id+"F2.wireOp",EDGE,"E7.right")])]})])],"derivedFrom":makeQuery(id+"F1.opExtrude","CAP_EDGE",EDGE,{"disambiguationData":[OSD([subQ0])],"isStart":false})});}
            var Q17;
            {var subQ0=sQuery(id+"F0.wireOp",EDGE,"E0.top");Q17=makeQuery(id+"F3.boolean.opBoolean","SPLIT",EDGE,{"disambiguationData":[TD([makeQuery(id+"F3.opExtrude","SWEPT_FACE",FACE,{"disambiguationData":[OSD([sQuery(id+"F2.wireOp",EDGE,"E6.right")])]})])],"derivedFrom":makeQuery(id+"F1.opExtrude","CAP_EDGE",EDGE,{"disambiguationData":[OSD([subQ0])],"isStart":false})});}
            var Q18;
            {var subQ0=sQuery(id+"F0.wireOp",EDGE,"E0.top");Q18=makeQuery(id+"F3.boolean.opBoolean","SPLIT",EDGE,{"disambiguationData":[TD([makeQuery(id+"F3.opExtrude","SWEPT_FACE",FACE,{"disambiguationData":[OSD([sQuery(id+"F2.wireOp",EDGE,"E5.right")])]})])],"derivedFrom":makeQuery(id+"F1.opExtrude","CAP_EDGE",EDGE,{"disambiguationData":[OSD([subQ0])],"isStart":false})});}
            var Q19;
            {var subQ0=sQuery(id+"F0.wireOp",EDGE,"E0.top");Q19=makeQuery(id+"F3.boolean.opBoolean","SPLIT",EDGE,{"disambiguationData":[TD([makeQuery(id+"F3.opExtrude","SWEPT_FACE",FACE,{"disambiguationData":[OSD([sQuery(id+"F2.wireOp",EDGE,"E4.right")])]})])],"derivedFrom":makeQuery(id+"F1.opExtrude","CAP_EDGE",EDGE,{"disambiguationData":[OSD([subQ0])],"isStart":false})});}
            var Q20;
            {var subQ0=sQuery(id+"F0.wireOp",EDGE,"E0.top");Q20=makeQuery(id+"F3.boolean.opBoolean","SPLIT",EDGE,{"disambiguationData":[TD([makeQuery(id+"F3.opExtrude","SWEPT_FACE",FACE,{"disambiguationData":[OSD([sQuery(id+"F2.wireOp",EDGE,"E3.right")])]})])],"derivedFrom":makeQuery(id+"F1.opExtrude","CAP_EDGE",EDGE,{"disambiguationData":[OSD([subQ0])],"isStart":false})});}
            var Q21;
            {var subQ0=sQuery(id+"F0.wireOp",EDGE,"E0.top");Q21=makeQuery(id+"F3.boolean.opBoolean","SPLIT",EDGE,{"disambiguationData":[TD([makeQuery(id+"F3.opExtrude","SWEPT_FACE",FACE,{"disambiguationData":[OSD([sQuery(id+"F2.wireOp",EDGE,"E2.right")])]})])],"derivedFrom":makeQuery(id+"F1.opExtrude","CAP_EDGE",EDGE,{"disambiguationData":[OSD([subQ0])],"isStart":false})});}
            var Q22;
            {var subQ0=sQuery(id+"F0.wireOp",EDGE,"E0.top");Q22=makeQuery(id+"F3.boolean.opBoolean","SPLIT",EDGE,{"disambiguationData":[TD([makeQuery(id+"F3.opExtrude","SWEPT_FACE",FACE,{"disambiguationData":[OSD([sQuery(id+"F2.wireOp",EDGE,"E1.right")])]})])],"derivedFrom":makeQuery(id+"F1.opExtrude","CAP_EDGE",EDGE,{"disambiguationData":[OSD([subQ0])],"isStart":false})});}
            var Q23;
            {var subQ0=sQuery(id+"F0.wireOp",EDGE,"E0.left");var subQ1=sQuery(id+"F0.wireOp",EDGE,"E0.top");Q23=makeQuery(id+"F3.boolean.opBoolean","SPLIT",EDGE,{"disambiguationData":[TD([makeQuery(id+"F1.opExtrude","SWEPT_FACE",FACE,{"disambiguationData":[OSD([subQ0])]})])],"derivedFrom":makeQuery(id+"F1.opExtrude","CAP_EDGE",EDGE,{"disambiguationData":[OSD([subQ1])],"isStart":false})});}
            var Q24;
            {var subQ0=sQuery(id+"F0.wireOp",EDGE,"E0.bottom");Q24=makeQuery(id+"F3.boolean.opBoolean","SPLIT",EDGE,{"disambiguationData":[TD([makeQuery(id+"F3.opExtrude","SWEPT_FACE",FACE,{"disambiguationData":[OSD([sQuery(id+"F2.wireOp",EDGE,"E7.right")])]})])],"derivedFrom":makeQuery(id+"F1.opExtrude","CAP_EDGE",EDGE,{"disambiguationData":[OSD([subQ0])],"isStart":false})});}
            var Q25;
            {var subQ0=sQuery(id+"F0.wireOp",EDGE,"E0.bottom");Q25=makeQuery(id+"F3.boolean.opBoolean","SPLIT",EDGE,{"disambiguationData":[TD([makeQuery(id+"F3.opExtrude","SWEPT_FACE",FACE,{"disambiguationData":[OSD([sQuery(id+"F2.wireOp",EDGE,"E6.right")])]})])],"derivedFrom":makeQuery(id+"F1.opExtrude","CAP_EDGE",EDGE,{"disambiguationData":[OSD([subQ0])],"isStart":false})});}
            var Q26;
            {var subQ0=sQuery(id+"F0.wireOp",EDGE,"E0.bottom");Q26=makeQuery(id+"F3.boolean.opBoolean","SPLIT",EDGE,{"disambiguationData":[TD([makeQuery(id+"F3.opExtrude","SWEPT_FACE",FACE,{"disambiguationData":[OSD([sQuery(id+"F2.wireOp",EDGE,"E5.right")])]})])],"derivedFrom":makeQuery(id+"F1.opExtrude","CAP_EDGE",EDGE,{"disambiguationData":[OSD([subQ0])],"isStart":false})});}
            var Q27;
            {var subQ0=sQuery(id+"F0.wireOp",EDGE,"E0.bottom");Q27=makeQuery(id+"F3.boolean.opBoolean","SPLIT",EDGE,{"disambiguationData":[TD([makeQuery(id+"F3.opExtrude","SWEPT_FACE",FACE,{"disambiguationData":[OSD([sQuery(id+"F2.wireOp",EDGE,"E4.right")])]})])],"derivedFrom":makeQuery(id+"F1.opExtrude","CAP_EDGE",EDGE,{"disambiguationData":[OSD([subQ0])],"isStart":false})});}
            var Q28;
            {var subQ0=sQuery(id+"F0.wireOp",EDGE,"E0.bottom");Q28=makeQuery(id+"F3.boolean.opBoolean","SPLIT",EDGE,{"disambiguationData":[TD([makeQuery(id+"F3.opExtrude","SWEPT_FACE",FACE,{"disambiguationData":[OSD([sQuery(id+"F2.wireOp",EDGE,"E3.right")])]})])],"derivedFrom":makeQuery(id+"F1.opExtrude","CAP_EDGE",EDGE,{"disambiguationData":[OSD([subQ0])],"isStart":false})});}
            var Q29;
            {var subQ0=sQuery(id+"F0.wireOp",EDGE,"E0.bottom");Q29=makeQuery(id+"F3.boolean.opBoolean","SPLIT",EDGE,{"disambiguationData":[TD([makeQuery(id+"F3.opExtrude","SWEPT_FACE",FACE,{"disambiguationData":[OSD([sQuery(id+"F2.wireOp",EDGE,"E2.right")])]})])],"derivedFrom":makeQuery(id+"F1.opExtrude","CAP_EDGE",EDGE,{"disambiguationData":[OSD([subQ0])],"isStart":false})});}
            var Q30;
            {var subQ0=sQuery(id+"F0.wireOp",EDGE,"E0.bottom");Q30=makeQuery(id+"F3.boolean.opBoolean","SPLIT",EDGE,{"disambiguationData":[TD([makeQuery(id+"F3.opExtrude","SWEPT_FACE",FACE,{"disambiguationData":[OSD([sQuery(id+"F2.wireOp",EDGE,"E1.right")])]})])],"derivedFrom":makeQuery(id+"F1.opExtrude","CAP_EDGE",EDGE,{"disambiguationData":[OSD([subQ0])],"isStart":false})});}
            var Q31;
            {var subQ0=sQuery(id+"F0.wireOp",EDGE,"E0.bottom");var subQ1=sQuery(id+"F0.wireOp",EDGE,"E0.left");Q31=makeQuery(id+"F3.boolean.opBoolean","SPLIT",EDGE,{"disambiguationData":[TD([makeQuery(id+"F1.opExtrude","SWEPT_FACE",FACE,{"disambiguationData":[OSD([subQ1])]})])],"derivedFrom":makeQuery(id+"F1.opExtrude","CAP_EDGE",EDGE,{"disambiguationData":[OSD([subQ0])],"isStart":false})});}
            fillet(context, id + "F10", {"entities" : qUnion([Q0, Q1, Q2, Q3, Q4, Q5, Q6, Q7, Q8, Q9, Q10, Q11, Q12, Q13, Q14, Q15, Q16, Q17, Q18, Q19, Q20, Q21, Q22, Q23, Q24, Q25, Q26, Q27, Q28, Q29, Q30, Q31]), "radius" : 12.7 * mm, "tangentPropagation" : true, "allowEdgeOverflow" : false});
        }
        {
            var Q0;
            Q0=makeQuery(id+"F5.opExtrude","CAP_EDGE",EDGE,{"disambiguationData":[OSD([sQuery(id+"F4.wireOp",EDGE,"E9.bottom")])],"isStart":false});
            var Q1;
            Q1=makeQuery(id+"F5.opExtrude","CAP_EDGE",EDGE,{"disambiguationData":[OSD([sQuery(id+"F4.wireOp",EDGE,"E10.bottom")])],"isStart":false});
            var Q2;
            Q2=makeQuery(id+"F5.opExtrude","CAP_EDGE",EDGE,{"disambiguationData":[OSD([sQuery(id+"F4.wireOp",EDGE,"E11.bottom")])],"isStart":false});
            var Q3;
            Q3=makeQuery(id+"F5.opExtrude","CAP_EDGE",EDGE,{"disambiguationData":[OSD([sQuery(id+"F4.wireOp",EDGE,"E12.bottom")])],"isStart":false});
            var Q4;
            Q4=makeQuery(id+"F5.opExtrude","CAP_EDGE",EDGE,{"disambiguationData":[OSD([sQuery(id+"F4.wireOp",EDGE,"E13.bottom")])],"isStart":false});
            var Q5;
            Q5=makeQuery(id+"F5.opExtrude","CAP_EDGE",EDGE,{"disambiguationData":[OSD([sQuery(id+"F4.wireOp",EDGE,"E14.bottom")])],"isStart":false});
            var Q6;
            Q6=makeQuery(id+"F5.opExtrude","CAP_EDGE",EDGE,{"disambiguationData":[OSD([sQuery(id+"F4.wireOp",EDGE,"E15.bottom")])],"isStart":false});
            var Q7;
            Q7=makeQuery(id+"F5.opExtrude","CAP_EDGE",EDGE,{"disambiguationData":[OSD([sQuery(id+"F4.wireOp",EDGE,"E16.bottom")])],"isStart":false});
            var Q8;
            Q8=makeQuery(id+"F9.opExtrude","CAP_EDGE",EDGE,{"disambiguationData":[OSD([sQuery(id+"F8.wireOp",EDGE,"E32.bottom")])],"isStart":false});
            var Q9;
            Q9=makeQuery(id+"F9.opExtrude","CAP_EDGE",EDGE,{"disambiguationData":[OSD([sQuery(id+"F8.wireOp",EDGE,"E31.bottom")])],"isStart":false});
            var Q10;
            Q10=makeQuery(id+"F9.opExtrude","CAP_EDGE",EDGE,{"disambiguationData":[OSD([sQuery(id+"F8.wireOp",EDGE,"E30.bottom")])],"isStart":false});
            var Q11;
            Q11=makeQuery(id+"F9.opExtrude","CAP_EDGE",EDGE,{"disambiguationData":[OSD([sQuery(id+"F8.wireOp",EDGE,"E29.bottom")])],"isStart":false});
            var Q12;
            Q12=makeQuery(id+"F9.opExtrude","CAP_EDGE",EDGE,{"disambiguationData":[OSD([sQuery(id+"F8.wireOp",EDGE,"E28.bottom")])],"isStart":false});
            var Q13;
            Q13=makeQuery(id+"F9.opExtrude","CAP_EDGE",EDGE,{"disambiguationData":[OSD([sQuery(id+"F8.wireOp",EDGE,"E27.bottom")])],"isStart":false});
            var Q14;
            Q14=makeQuery(id+"F9.opExtrude","CAP_EDGE",EDGE,{"disambiguationData":[OSD([sQuery(id+"F8.wireOp",EDGE,"E26.bottom")])],"isStart":false});
            var Q15;
            Q15=makeQuery(id+"F9.opExtrude","CAP_EDGE",EDGE,{"disambiguationData":[OSD([sQuery(id+"F8.wireOp",EDGE,"E25.bottom")])],"isStart":false});
            var Q16;
            Q16=makeQuery(id+"F7.opExtrude","CAP_EDGE",EDGE,{"disambiguationData":[OSD([sQuery(id+"F6.wireOp",EDGE,"E17.bottom")])],"isStart":false});
            var Q17;
            Q17=makeQuery(id+"F7.opExtrude","CAP_EDGE",EDGE,{"disambiguationData":[OSD([sQuery(id+"F6.wireOp",EDGE,"E18.bottom")])],"isStart":false});
            var Q18;
            Q18=makeQuery(id+"F7.opExtrude","CAP_EDGE",EDGE,{"disambiguationData":[OSD([sQuery(id+"F6.wireOp",EDGE,"E19.bottom")])],"isStart":false});
            var Q19;
            Q19=makeQuery(id+"F7.opExtrude","CAP_EDGE",EDGE,{"disambiguationData":[OSD([sQuery(id+"F6.wireOp",EDGE,"E20.bottom")])],"isStart":false});
            var Q20;
            Q20=makeQuery(id+"F7.opExtrude","CAP_EDGE",EDGE,{"disambiguationData":[OSD([sQuery(id+"F6.wireOp",EDGE,"E21.bottom")])],"isStart":false});
            var Q21;
            Q21=makeQuery(id+"F7.opExtrude","CAP_EDGE",EDGE,{"disambiguationData":[OSD([sQuery(id+"F6.wireOp",EDGE,"E22.bottom")])],"isStart":false});
            var Q22;
            Q22=makeQuery(id+"F7.opExtrude","CAP_EDGE",EDGE,{"disambiguationData":[OSD([sQuery(id+"F6.wireOp",EDGE,"E23.bottom")])],"isStart":false});
            var Q23;
            Q23=makeQuery(id+"F7.opExtrude","CAP_EDGE",EDGE,{"disambiguationData":[OSD([sQuery(id+"F6.wireOp",EDGE,"E24.bottom")])],"isStart":false});
            var Q24;
            Q24=makeQuery(id+"F9.opExtrude","CAP_EDGE",EDGE,{"disambiguationData":[OSD([sQuery(id+"F8.wireOp",EDGE,"E32.top")])],"isStart":false});
            var Q25;
            Q25=makeQuery(id+"F9.opExtrude","CAP_EDGE",EDGE,{"disambiguationData":[OSD([sQuery(id+"F8.wireOp",EDGE,"E31.top")])],"isStart":false});
            var Q26;
            Q26=makeQuery(id+"F9.opExtrude","CAP_EDGE",EDGE,{"disambiguationData":[OSD([sQuery(id+"F8.wireOp",EDGE,"E30.top")])],"isStart":false});
            var Q27;
            Q27=makeQuery(id+"F9.opExtrude","CAP_EDGE",EDGE,{"disambiguationData":[OSD([sQuery(id+"F8.wireOp",EDGE,"E29.top")])],"isStart":false});
            var Q28;
            Q28=makeQuery(id+"F9.opExtrude","CAP_EDGE",EDGE,{"disambiguationData":[OSD([sQuery(id+"F8.wireOp",EDGE,"E28.top")])],"isStart":false});
            var Q29;
            Q29=makeQuery(id+"F9.opExtrude","CAP_EDGE",EDGE,{"disambiguationData":[OSD([sQuery(id+"F8.wireOp",EDGE,"E27.top")])],"isStart":false});
            var Q30;
            Q30=makeQuery(id+"F9.opExtrude","CAP_EDGE",EDGE,{"disambiguationData":[OSD([sQuery(id+"F8.wireOp",EDGE,"E26.top")])],"isStart":false});
            var Q31;
            Q31=makeQuery(id+"F9.opExtrude","CAP_EDGE",EDGE,{"disambiguationData":[OSD([sQuery(id+"F8.wireOp",EDGE,"E25.top")])],"isStart":false});
            fillet(context, id + "F11", {"entities" : qUnion([Q0, Q1, Q2, Q3, Q4, Q5, Q6, Q7, Q8, Q9, Q10, Q11, Q12, Q13, Q14, Q15, Q16, Q17, Q18, Q19, Q20, Q21, Q22, Q23, Q24, Q25, Q26, Q27, Q28, Q29, Q30, Q31]), "radius" : 15.24 * mm, "tangentPropagation" : true, "allowEdgeOverflow" : false});
        }
        {
            var Q0;
            Q0=makeQuery(id+"F11.opFillet","BLEND_EDGE",EDGE,{"blendedFrom":[makeQuery(id+"F5.opExtrude","CAP_EDGE",EDGE,{"disambiguationData":[OSD([sQuery(id+"F4.wireOp",EDGE,"E9.bottom")])],"isStart":false}),makeQuery(id+"F9.boolean.opBoolean","MERGE",FACE,{"derivedFrom":[makeQuery(id+"F7.boolean.opBoolean","MERGE",FACE,{"derivedFrom":[makeQuery(id+"F5.boolean.opBoolean","MERGE",FACE,{"derivedFrom":[makeQuery(id+"F3.opExtrude","SWEPT_FACE",FACE,{"disambiguationData":[OSD([sQuery(id+"F2.wireOp",EDGE,"E1.left")])]}),makeQuery(id+"F5.opExtrude","SWEPT_FACE",FACE,{"disambiguationData":[OSD([sQuery(id+"F4.wireOp",EDGE,"E9.left")])]})]}),makeQuery(id+"F7.opExtrude","SWEPT_FACE",FACE,{"disambiguationData":[OSD([sQuery(id+"F6.wireOp",EDGE,"E17.left")])]})]}),makeQuery(id+"F9.opExtrude","SWEPT_FACE",FACE,{"disambiguationData":[OSD([sQuery(id+"F8.wireOp",EDGE,"E32.right")])]})]})],"blendedInto":[makeQuery(id+"F9.boolean.opBoolean","MERGE",FACE,{"derivedFrom":[makeQuery(id+"F7.boolean.opBoolean","MERGE",FACE,{"derivedFrom":[makeQuery(id+"F5.boolean.opBoolean","MERGE",FACE,{"derivedFrom":[makeQuery(id+"F3.opExtrude","SWEPT_FACE",FACE,{"disambiguationData":[OSD([sQuery(id+"F2.wireOp",EDGE,"E1.left")])]}),makeQuery(id+"F5.opExtrude","SWEPT_FACE",FACE,{"disambiguationData":[OSD([sQuery(id+"F4.wireOp",EDGE,"E9.left")])]})]}),makeQuery(id+"F7.opExtrude","SWEPT_FACE",FACE,{"disambiguationData":[OSD([sQuery(id+"F6.wireOp",EDGE,"E17.left")])]})]}),makeQuery(id+"F9.opExtrude","SWEPT_FACE",FACE,{"disambiguationData":[OSD([sQuery(id+"F8.wireOp",EDGE,"E32.right")])]})]})]});
            var Q1;
            Q1=makeQuery(id+"F11.opFillet","BLEND_EDGE",EDGE,{"blendedFrom":[makeQuery(id+"F9.opExtrude","CAP_EDGE",EDGE,{"disambiguationData":[OSD([sQuery(id+"F8.wireOp",EDGE,"E32.bottom")])],"isStart":false}),makeQuery(id+"F9.boolean.opBoolean","MERGE",FACE,{"derivedFrom":[makeQuery(id+"F7.boolean.opBoolean","MERGE",FACE,{"derivedFrom":[makeQuery(id+"F5.boolean.opBoolean","MERGE",FACE,{"derivedFrom":[makeQuery(id+"F3.opExtrude","SWEPT_FACE",FACE,{"disambiguationData":[OSD([sQuery(id+"F2.wireOp",EDGE,"E1.left")])]}),makeQuery(id+"F5.opExtrude","SWEPT_FACE",FACE,{"disambiguationData":[OSD([sQuery(id+"F4.wireOp",EDGE,"E9.left")])]})]}),makeQuery(id+"F7.opExtrude","SWEPT_FACE",FACE,{"disambiguationData":[OSD([sQuery(id+"F6.wireOp",EDGE,"E17.left")])]})]}),makeQuery(id+"F9.opExtrude","SWEPT_FACE",FACE,{"disambiguationData":[OSD([sQuery(id+"F8.wireOp",EDGE,"E32.right")])]})]})],"blendedInto":[makeQuery(id+"F9.boolean.opBoolean","MERGE",FACE,{"derivedFrom":[makeQuery(id+"F7.boolean.opBoolean","MERGE",FACE,{"derivedFrom":[makeQuery(id+"F5.boolean.opBoolean","MERGE",FACE,{"derivedFrom":[makeQuery(id+"F3.opExtrude","SWEPT_FACE",FACE,{"disambiguationData":[OSD([sQuery(id+"F2.wireOp",EDGE,"E1.left")])]}),makeQuery(id+"F5.opExtrude","SWEPT_FACE",FACE,{"disambiguationData":[OSD([sQuery(id+"F4.wireOp",EDGE,"E9.left")])]})]}),makeQuery(id+"F7.opExtrude","SWEPT_FACE",FACE,{"disambiguationData":[OSD([sQuery(id+"F6.wireOp",EDGE,"E17.left")])]})]}),makeQuery(id+"F9.opExtrude","SWEPT_FACE",FACE,{"disambiguationData":[OSD([sQuery(id+"F8.wireOp",EDGE,"E32.right")])]})]})]});
            var Q2;
            Q2=makeQuery(id+"F11.opFillet","BLEND_EDGE",EDGE,{"blendedFrom":[makeQuery(id+"F5.opExtrude","CAP_EDGE",EDGE,{"disambiguationData":[OSD([sQuery(id+"F4.wireOp",EDGE,"E9.bottom")])],"isStart":false}),makeQuery(id+"F9.boolean.opBoolean","MERGE",FACE,{"derivedFrom":[makeQuery(id+"F7.boolean.opBoolean","MERGE",FACE,{"derivedFrom":[makeQuery(id+"F5.boolean.opBoolean","MERGE",FACE,{"derivedFrom":[makeQuery(id+"F3.opExtrude","SWEPT_FACE",FACE,{"disambiguationData":[OSD([sQuery(id+"F2.wireOp",EDGE,"E1.right")])]}),makeQuery(id+"F5.opExtrude","SWEPT_FACE",FACE,{"disambiguationData":[OSD([sQuery(id+"F4.wireOp",EDGE,"E9.right")])]})]}),makeQuery(id+"F7.opExtrude","SWEPT_FACE",FACE,{"disambiguationData":[OSD([sQuery(id+"F6.wireOp",EDGE,"E17.right")])]})]}),makeQuery(id+"F9.opExtrude","SWEPT_FACE",FACE,{"disambiguationData":[OSD([sQuery(id+"F8.wireOp",EDGE,"E32.left")])]})]})],"blendedInto":[makeQuery(id+"F9.boolean.opBoolean","MERGE",FACE,{"derivedFrom":[makeQuery(id+"F7.boolean.opBoolean","MERGE",FACE,{"derivedFrom":[makeQuery(id+"F5.boolean.opBoolean","MERGE",FACE,{"derivedFrom":[makeQuery(id+"F3.opExtrude","SWEPT_FACE",FACE,{"disambiguationData":[OSD([sQuery(id+"F2.wireOp",EDGE,"E1.right")])]}),makeQuery(id+"F5.opExtrude","SWEPT_FACE",FACE,{"disambiguationData":[OSD([sQuery(id+"F4.wireOp",EDGE,"E9.right")])]})]}),makeQuery(id+"F7.opExtrude","SWEPT_FACE",FACE,{"disambiguationData":[OSD([sQuery(id+"F6.wireOp",EDGE,"E17.right")])]})]}),makeQuery(id+"F9.opExtrude","SWEPT_FACE",FACE,{"disambiguationData":[OSD([sQuery(id+"F8.wireOp",EDGE,"E32.left")])]})]})]});
            var Q3;
            Q3=makeQuery(id+"F11.opFillet","BLEND_EDGE",EDGE,{"blendedFrom":[makeQuery(id+"F9.opExtrude","CAP_EDGE",EDGE,{"disambiguationData":[OSD([sQuery(id+"F8.wireOp",EDGE,"E32.bottom")])],"isStart":false}),makeQuery(id+"F9.boolean.opBoolean","MERGE",FACE,{"derivedFrom":[makeQuery(id+"F7.boolean.opBoolean","MERGE",FACE,{"derivedFrom":[makeQuery(id+"F5.boolean.opBoolean","MERGE",FACE,{"derivedFrom":[makeQuery(id+"F3.opExtrude","SWEPT_FACE",FACE,{"disambiguationData":[OSD([sQuery(id+"F2.wireOp",EDGE,"E1.right")])]}),makeQuery(id+"F5.opExtrude","SWEPT_FACE",FACE,{"disambiguationData":[OSD([sQuery(id+"F4.wireOp",EDGE,"E9.right")])]})]}),makeQuery(id+"F7.opExtrude","SWEPT_FACE",FACE,{"disambiguationData":[OSD([sQuery(id+"F6.wireOp",EDGE,"E17.right")])]})]}),makeQuery(id+"F9.opExtrude","SWEPT_FACE",FACE,{"disambiguationData":[OSD([sQuery(id+"F8.wireOp",EDGE,"E32.left")])]})]})],"blendedInto":[makeQuery(id+"F9.boolean.opBoolean","MERGE",FACE,{"derivedFrom":[makeQuery(id+"F7.boolean.opBoolean","MERGE",FACE,{"derivedFrom":[makeQuery(id+"F5.boolean.opBoolean","MERGE",FACE,{"derivedFrom":[makeQuery(id+"F3.opExtrude","SWEPT_FACE",FACE,{"disambiguationData":[OSD([sQuery(id+"F2.wireOp",EDGE,"E1.right")])]}),makeQuery(id+"F5.opExtrude","SWEPT_FACE",FACE,{"disambiguationData":[OSD([sQuery(id+"F4.wireOp",EDGE,"E9.right")])]})]}),makeQuery(id+"F7.opExtrude","SWEPT_FACE",FACE,{"disambiguationData":[OSD([sQuery(id+"F6.wireOp",EDGE,"E17.right")])]})]}),makeQuery(id+"F9.opExtrude","SWEPT_FACE",FACE,{"disambiguationData":[OSD([sQuery(id+"F8.wireOp",EDGE,"E32.left")])]})]})]});
            var Q4;
            Q4=makeQuery(id+"F11.opFillet","BLEND_EDGE",EDGE,{"blendedFrom":[makeQuery(id+"F5.opExtrude","CAP_EDGE",EDGE,{"disambiguationData":[OSD([sQuery(id+"F4.wireOp",EDGE,"E10.bottom")])],"isStart":false}),makeQuery(id+"F9.boolean.opBoolean","MERGE",FACE,{"derivedFrom":[makeQuery(id+"F7.boolean.opBoolean","MERGE",FACE,{"derivedFrom":[makeQuery(id+"F5.boolean.opBoolean","MERGE",FACE,{"derivedFrom":[makeQuery(id+"F3.opExtrude","SWEPT_FACE",FACE,{"disambiguationData":[OSD([sQuery(id+"F2.wireOp",EDGE,"E2.left")])]}),makeQuery(id+"F5.opExtrude","SWEPT_FACE",FACE,{"disambiguationData":[OSD([sQuery(id+"F4.wireOp",EDGE,"E10.left")])]})]}),makeQuery(id+"F7.opExtrude","SWEPT_FACE",FACE,{"disambiguationData":[OSD([sQuery(id+"F6.wireOp",EDGE,"E18.left")])]})]}),makeQuery(id+"F9.opExtrude","SWEPT_FACE",FACE,{"disambiguationData":[OSD([sQuery(id+"F8.wireOp",EDGE,"E31.right")])]})]})],"blendedInto":[makeQuery(id+"F9.boolean.opBoolean","MERGE",FACE,{"derivedFrom":[makeQuery(id+"F7.boolean.opBoolean","MERGE",FACE,{"derivedFrom":[makeQuery(id+"F5.boolean.opBoolean","MERGE",FACE,{"derivedFrom":[makeQuery(id+"F3.opExtrude","SWEPT_FACE",FACE,{"disambiguationData":[OSD([sQuery(id+"F2.wireOp",EDGE,"E2.left")])]}),makeQuery(id+"F5.opExtrude","SWEPT_FACE",FACE,{"disambiguationData":[OSD([sQuery(id+"F4.wireOp",EDGE,"E10.left")])]})]}),makeQuery(id+"F7.opExtrude","SWEPT_FACE",FACE,{"disambiguationData":[OSD([sQuery(id+"F6.wireOp",EDGE,"E18.left")])]})]}),makeQuery(id+"F9.opExtrude","SWEPT_FACE",FACE,{"disambiguationData":[OSD([sQuery(id+"F8.wireOp",EDGE,"E31.right")])]})]})]});
            var Q5;
            Q5=makeQuery(id+"F11.opFillet","BLEND_EDGE",EDGE,{"blendedFrom":[makeQuery(id+"F5.opExtrude","CAP_EDGE",EDGE,{"disambiguationData":[OSD([sQuery(id+"F4.wireOp",EDGE,"E10.bottom")])],"isStart":false}),makeQuery(id+"F9.boolean.opBoolean","MERGE",FACE,{"derivedFrom":[makeQuery(id+"F7.boolean.opBoolean","MERGE",FACE,{"derivedFrom":[makeQuery(id+"F5.boolean.opBoolean","MERGE",FACE,{"derivedFrom":[makeQuery(id+"F3.opExtrude","SWEPT_FACE",FACE,{"disambiguationData":[OSD([sQuery(id+"F2.wireOp",EDGE,"E2.right")])]}),makeQuery(id+"F5.opExtrude","SWEPT_FACE",FACE,{"disambiguationData":[OSD([sQuery(id+"F4.wireOp",EDGE,"E10.right")])]})]}),makeQuery(id+"F7.opExtrude","SWEPT_FACE",FACE,{"disambiguationData":[OSD([sQuery(id+"F6.wireOp",EDGE,"E18.right")])]})]}),makeQuery(id+"F9.opExtrude","SWEPT_FACE",FACE,{"disambiguationData":[OSD([sQuery(id+"F8.wireOp",EDGE,"E31.left")])]})]})],"blendedInto":[makeQuery(id+"F9.boolean.opBoolean","MERGE",FACE,{"derivedFrom":[makeQuery(id+"F7.boolean.opBoolean","MERGE",FACE,{"derivedFrom":[makeQuery(id+"F5.boolean.opBoolean","MERGE",FACE,{"derivedFrom":[makeQuery(id+"F3.opExtrude","SWEPT_FACE",FACE,{"disambiguationData":[OSD([sQuery(id+"F2.wireOp",EDGE,"E2.right")])]}),makeQuery(id+"F5.opExtrude","SWEPT_FACE",FACE,{"disambiguationData":[OSD([sQuery(id+"F4.wireOp",EDGE,"E10.right")])]})]}),makeQuery(id+"F7.opExtrude","SWEPT_FACE",FACE,{"disambiguationData":[OSD([sQuery(id+"F6.wireOp",EDGE,"E18.right")])]})]}),makeQuery(id+"F9.opExtrude","SWEPT_FACE",FACE,{"disambiguationData":[OSD([sQuery(id+"F8.wireOp",EDGE,"E31.left")])]})]})]});
            var Q6;
            Q6=makeQuery(id+"F11.opFillet","BLEND_EDGE",EDGE,{"blendedFrom":[makeQuery(id+"F9.opExtrude","CAP_EDGE",EDGE,{"disambiguationData":[OSD([sQuery(id+"F8.wireOp",EDGE,"E31.bottom")])],"isStart":false}),makeQuery(id+"F9.boolean.opBoolean","MERGE",FACE,{"derivedFrom":[makeQuery(id+"F7.boolean.opBoolean","MERGE",FACE,{"derivedFrom":[makeQuery(id+"F5.boolean.opBoolean","MERGE",FACE,{"derivedFrom":[makeQuery(id+"F3.opExtrude","SWEPT_FACE",FACE,{"disambiguationData":[OSD([sQuery(id+"F2.wireOp",EDGE,"E2.left")])]}),makeQuery(id+"F5.opExtrude","SWEPT_FACE",FACE,{"disambiguationData":[OSD([sQuery(id+"F4.wireOp",EDGE,"E10.left")])]})]}),makeQuery(id+"F7.opExtrude","SWEPT_FACE",FACE,{"disambiguationData":[OSD([sQuery(id+"F6.wireOp",EDGE,"E18.left")])]})]}),makeQuery(id+"F9.opExtrude","SWEPT_FACE",FACE,{"disambiguationData":[OSD([sQuery(id+"F8.wireOp",EDGE,"E31.right")])]})]})],"blendedInto":[makeQuery(id+"F9.boolean.opBoolean","MERGE",FACE,{"derivedFrom":[makeQuery(id+"F7.boolean.opBoolean","MERGE",FACE,{"derivedFrom":[makeQuery(id+"F5.boolean.opBoolean","MERGE",FACE,{"derivedFrom":[makeQuery(id+"F3.opExtrude","SWEPT_FACE",FACE,{"disambiguationData":[OSD([sQuery(id+"F2.wireOp",EDGE,"E2.left")])]}),makeQuery(id+"F5.opExtrude","SWEPT_FACE",FACE,{"disambiguationData":[OSD([sQuery(id+"F4.wireOp",EDGE,"E10.left")])]})]}),makeQuery(id+"F7.opExtrude","SWEPT_FACE",FACE,{"disambiguationData":[OSD([sQuery(id+"F6.wireOp",EDGE,"E18.left")])]})]}),makeQuery(id+"F9.opExtrude","SWEPT_FACE",FACE,{"disambiguationData":[OSD([sQuery(id+"F8.wireOp",EDGE,"E31.right")])]})]})]});
            var Q7;
            Q7=makeQuery(id+"F11.opFillet","BLEND_EDGE",EDGE,{"blendedFrom":[makeQuery(id+"F9.opExtrude","CAP_EDGE",EDGE,{"disambiguationData":[OSD([sQuery(id+"F8.wireOp",EDGE,"E31.bottom")])],"isStart":false}),makeQuery(id+"F9.boolean.opBoolean","MERGE",FACE,{"derivedFrom":[makeQuery(id+"F7.boolean.opBoolean","MERGE",FACE,{"derivedFrom":[makeQuery(id+"F5.boolean.opBoolean","MERGE",FACE,{"derivedFrom":[makeQuery(id+"F3.opExtrude","SWEPT_FACE",FACE,{"disambiguationData":[OSD([sQuery(id+"F2.wireOp",EDGE,"E2.right")])]}),makeQuery(id+"F5.opExtrude","SWEPT_FACE",FACE,{"disambiguationData":[OSD([sQuery(id+"F4.wireOp",EDGE,"E10.right")])]})]}),makeQuery(id+"F7.opExtrude","SWEPT_FACE",FACE,{"disambiguationData":[OSD([sQuery(id+"F6.wireOp",EDGE,"E18.right")])]})]}),makeQuery(id+"F9.opExtrude","SWEPT_FACE",FACE,{"disambiguationData":[OSD([sQuery(id+"F8.wireOp",EDGE,"E31.left")])]})]})],"blendedInto":[makeQuery(id+"F9.boolean.opBoolean","MERGE",FACE,{"derivedFrom":[makeQuery(id+"F7.boolean.opBoolean","MERGE",FACE,{"derivedFrom":[makeQuery(id+"F5.boolean.opBoolean","MERGE",FACE,{"derivedFrom":[makeQuery(id+"F3.opExtrude","SWEPT_FACE",FACE,{"disambiguationData":[OSD([sQuery(id+"F2.wireOp",EDGE,"E2.right")])]}),makeQuery(id+"F5.opExtrude","SWEPT_FACE",FACE,{"disambiguationData":[OSD([sQuery(id+"F4.wireOp",EDGE,"E10.right")])]})]}),makeQuery(id+"F7.opExtrude","SWEPT_FACE",FACE,{"disambiguationData":[OSD([sQuery(id+"F6.wireOp",EDGE,"E18.right")])]})]}),makeQuery(id+"F9.opExtrude","SWEPT_FACE",FACE,{"disambiguationData":[OSD([sQuery(id+"F8.wireOp",EDGE,"E31.left")])]})]})]});
            var Q8;
            Q8=makeQuery(id+"F11.opFillet","BLEND_EDGE",EDGE,{"blendedFrom":[makeQuery(id+"F5.opExtrude","CAP_EDGE",EDGE,{"disambiguationData":[OSD([sQuery(id+"F4.wireOp",EDGE,"E11.bottom")])],"isStart":false}),makeQuery(id+"F9.boolean.opBoolean","MERGE",FACE,{"derivedFrom":[makeQuery(id+"F7.boolean.opBoolean","MERGE",FACE,{"derivedFrom":[makeQuery(id+"F5.boolean.opBoolean","MERGE",FACE,{"derivedFrom":[makeQuery(id+"F3.opExtrude","SWEPT_FACE",FACE,{"disambiguationData":[OSD([sQuery(id+"F2.wireOp",EDGE,"E3.left")])]}),makeQuery(id+"F5.opExtrude","SWEPT_FACE",FACE,{"disambiguationData":[OSD([sQuery(id+"F4.wireOp",EDGE,"E11.left")])]})]}),makeQuery(id+"F7.opExtrude","SWEPT_FACE",FACE,{"disambiguationData":[OSD([sQuery(id+"F6.wireOp",EDGE,"E19.left")])]})]}),makeQuery(id+"F9.opExtrude","SWEPT_FACE",FACE,{"disambiguationData":[OSD([sQuery(id+"F8.wireOp",EDGE,"E30.right")])]})]})],"blendedInto":[makeQuery(id+"F9.boolean.opBoolean","MERGE",FACE,{"derivedFrom":[makeQuery(id+"F7.boolean.opBoolean","MERGE",FACE,{"derivedFrom":[makeQuery(id+"F5.boolean.opBoolean","MERGE",FACE,{"derivedFrom":[makeQuery(id+"F3.opExtrude","SWEPT_FACE",FACE,{"disambiguationData":[OSD([sQuery(id+"F2.wireOp",EDGE,"E3.left")])]}),makeQuery(id+"F5.opExtrude","SWEPT_FACE",FACE,{"disambiguationData":[OSD([sQuery(id+"F4.wireOp",EDGE,"E11.left")])]})]}),makeQuery(id+"F7.opExtrude","SWEPT_FACE",FACE,{"disambiguationData":[OSD([sQuery(id+"F6.wireOp",EDGE,"E19.left")])]})]}),makeQuery(id+"F9.opExtrude","SWEPT_FACE",FACE,{"disambiguationData":[OSD([sQuery(id+"F8.wireOp",EDGE,"E30.right")])]})]})]});
            var Q9;
            Q9=makeQuery(id+"F11.opFillet","BLEND_EDGE",EDGE,{"blendedFrom":[makeQuery(id+"F5.opExtrude","CAP_EDGE",EDGE,{"disambiguationData":[OSD([sQuery(id+"F4.wireOp",EDGE,"E11.bottom")])],"isStart":false}),makeQuery(id+"F9.boolean.opBoolean","MERGE",FACE,{"derivedFrom":[makeQuery(id+"F7.boolean.opBoolean","MERGE",FACE,{"derivedFrom":[makeQuery(id+"F5.boolean.opBoolean","MERGE",FACE,{"derivedFrom":[makeQuery(id+"F3.opExtrude","SWEPT_FACE",FACE,{"disambiguationData":[OSD([sQuery(id+"F2.wireOp",EDGE,"E3.right")])]}),makeQuery(id+"F5.opExtrude","SWEPT_FACE",FACE,{"disambiguationData":[OSD([sQuery(id+"F4.wireOp",EDGE,"E11.right")])]})]}),makeQuery(id+"F7.opExtrude","SWEPT_FACE",FACE,{"disambiguationData":[OSD([sQuery(id+"F6.wireOp",EDGE,"E19.right")])]})]}),makeQuery(id+"F9.opExtrude","SWEPT_FACE",FACE,{"disambiguationData":[OSD([sQuery(id+"F8.wireOp",EDGE,"E30.left")])]})]})],"blendedInto":[makeQuery(id+"F9.boolean.opBoolean","MERGE",FACE,{"derivedFrom":[makeQuery(id+"F7.boolean.opBoolean","MERGE",FACE,{"derivedFrom":[makeQuery(id+"F5.boolean.opBoolean","MERGE",FACE,{"derivedFrom":[makeQuery(id+"F3.opExtrude","SWEPT_FACE",FACE,{"disambiguationData":[OSD([sQuery(id+"F2.wireOp",EDGE,"E3.right")])]}),makeQuery(id+"F5.opExtrude","SWEPT_FACE",FACE,{"disambiguationData":[OSD([sQuery(id+"F4.wireOp",EDGE,"E11.right")])]})]}),makeQuery(id+"F7.opExtrude","SWEPT_FACE",FACE,{"disambiguationData":[OSD([sQuery(id+"F6.wireOp",EDGE,"E19.right")])]})]}),makeQuery(id+"F9.opExtrude","SWEPT_FACE",FACE,{"disambiguationData":[OSD([sQuery(id+"F8.wireOp",EDGE,"E30.left")])]})]})]});
            var Q10;
            Q10=makeQuery(id+"F11.opFillet","BLEND_EDGE",EDGE,{"blendedFrom":[makeQuery(id+"F9.opExtrude","CAP_EDGE",EDGE,{"disambiguationData":[OSD([sQuery(id+"F8.wireOp",EDGE,"E30.bottom")])],"isStart":false}),makeQuery(id+"F9.boolean.opBoolean","MERGE",FACE,{"derivedFrom":[makeQuery(id+"F7.boolean.opBoolean","MERGE",FACE,{"derivedFrom":[makeQuery(id+"F5.boolean.opBoolean","MERGE",FACE,{"derivedFrom":[makeQuery(id+"F3.opExtrude","SWEPT_FACE",FACE,{"disambiguationData":[OSD([sQuery(id+"F2.wireOp",EDGE,"E3.right")])]}),makeQuery(id+"F5.opExtrude","SWEPT_FACE",FACE,{"disambiguationData":[OSD([sQuery(id+"F4.wireOp",EDGE,"E11.right")])]})]}),makeQuery(id+"F7.opExtrude","SWEPT_FACE",FACE,{"disambiguationData":[OSD([sQuery(id+"F6.wireOp",EDGE,"E19.right")])]})]}),makeQuery(id+"F9.opExtrude","SWEPT_FACE",FACE,{"disambiguationData":[OSD([sQuery(id+"F8.wireOp",EDGE,"E30.left")])]})]})],"blendedInto":[makeQuery(id+"F9.boolean.opBoolean","MERGE",FACE,{"derivedFrom":[makeQuery(id+"F7.boolean.opBoolean","MERGE",FACE,{"derivedFrom":[makeQuery(id+"F5.boolean.opBoolean","MERGE",FACE,{"derivedFrom":[makeQuery(id+"F3.opExtrude","SWEPT_FACE",FACE,{"disambiguationData":[OSD([sQuery(id+"F2.wireOp",EDGE,"E3.right")])]}),makeQuery(id+"F5.opExtrude","SWEPT_FACE",FACE,{"disambiguationData":[OSD([sQuery(id+"F4.wireOp",EDGE,"E11.right")])]})]}),makeQuery(id+"F7.opExtrude","SWEPT_FACE",FACE,{"disambiguationData":[OSD([sQuery(id+"F6.wireOp",EDGE,"E19.right")])]})]}),makeQuery(id+"F9.opExtrude","SWEPT_FACE",FACE,{"disambiguationData":[OSD([sQuery(id+"F8.wireOp",EDGE,"E30.left")])]})]})]});
            var Q11;
            Q11=makeQuery(id+"F11.opFillet","BLEND_EDGE",EDGE,{"blendedFrom":[makeQuery(id+"F9.opExtrude","CAP_EDGE",EDGE,{"disambiguationData":[OSD([sQuery(id+"F8.wireOp",EDGE,"E30.bottom")])],"isStart":false}),makeQuery(id+"F9.boolean.opBoolean","MERGE",FACE,{"derivedFrom":[makeQuery(id+"F7.boolean.opBoolean","MERGE",FACE,{"derivedFrom":[makeQuery(id+"F5.boolean.opBoolean","MERGE",FACE,{"derivedFrom":[makeQuery(id+"F3.opExtrude","SWEPT_FACE",FACE,{"disambiguationData":[OSD([sQuery(id+"F2.wireOp",EDGE,"E3.left")])]}),makeQuery(id+"F5.opExtrude","SWEPT_FACE",FACE,{"disambiguationData":[OSD([sQuery(id+"F4.wireOp",EDGE,"E11.left")])]})]}),makeQuery(id+"F7.opExtrude","SWEPT_FACE",FACE,{"disambiguationData":[OSD([sQuery(id+"F6.wireOp",EDGE,"E19.left")])]})]}),makeQuery(id+"F9.opExtrude","SWEPT_FACE",FACE,{"disambiguationData":[OSD([sQuery(id+"F8.wireOp",EDGE,"E30.right")])]})]})],"blendedInto":[makeQuery(id+"F9.boolean.opBoolean","MERGE",FACE,{"derivedFrom":[makeQuery(id+"F7.boolean.opBoolean","MERGE",FACE,{"derivedFrom":[makeQuery(id+"F5.boolean.opBoolean","MERGE",FACE,{"derivedFrom":[makeQuery(id+"F3.opExtrude","SWEPT_FACE",FACE,{"disambiguationData":[OSD([sQuery(id+"F2.wireOp",EDGE,"E3.left")])]}),makeQuery(id+"F5.opExtrude","SWEPT_FACE",FACE,{"disambiguationData":[OSD([sQuery(id+"F4.wireOp",EDGE,"E11.left")])]})]}),makeQuery(id+"F7.opExtrude","SWEPT_FACE",FACE,{"disambiguationData":[OSD([sQuery(id+"F6.wireOp",EDGE,"E19.left")])]})]}),makeQuery(id+"F9.opExtrude","SWEPT_FACE",FACE,{"disambiguationData":[OSD([sQuery(id+"F8.wireOp",EDGE,"E30.right")])]})]})]});
            var Q12;
            Q12=makeQuery(id+"F11.opFillet","BLEND_EDGE",EDGE,{"blendedFrom":[makeQuery(id+"F5.opExtrude","CAP_EDGE",EDGE,{"disambiguationData":[OSD([sQuery(id+"F4.wireOp",EDGE,"E12.bottom")])],"isStart":false}),makeQuery(id+"F9.boolean.opBoolean","MERGE",FACE,{"derivedFrom":[makeQuery(id+"F7.boolean.opBoolean","MERGE",FACE,{"derivedFrom":[makeQuery(id+"F5.boolean.opBoolean","MERGE",FACE,{"derivedFrom":[makeQuery(id+"F3.opExtrude","SWEPT_FACE",FACE,{"disambiguationData":[OSD([sQuery(id+"F2.wireOp",EDGE,"E4.left")])]}),makeQuery(id+"F5.opExtrude","SWEPT_FACE",FACE,{"disambiguationData":[OSD([sQuery(id+"F4.wireOp",EDGE,"E12.left")])]})]}),makeQuery(id+"F7.opExtrude","SWEPT_FACE",FACE,{"disambiguationData":[OSD([sQuery(id+"F6.wireOp",EDGE,"E20.left")])]})]}),makeQuery(id+"F9.opExtrude","SWEPT_FACE",FACE,{"disambiguationData":[OSD([sQuery(id+"F8.wireOp",EDGE,"E29.right")])]})]})],"blendedInto":[makeQuery(id+"F9.boolean.opBoolean","MERGE",FACE,{"derivedFrom":[makeQuery(id+"F7.boolean.opBoolean","MERGE",FACE,{"derivedFrom":[makeQuery(id+"F5.boolean.opBoolean","MERGE",FACE,{"derivedFrom":[makeQuery(id+"F3.opExtrude","SWEPT_FACE",FACE,{"disambiguationData":[OSD([sQuery(id+"F2.wireOp",EDGE,"E4.left")])]}),makeQuery(id+"F5.opExtrude","SWEPT_FACE",FACE,{"disambiguationData":[OSD([sQuery(id+"F4.wireOp",EDGE,"E12.left")])]})]}),makeQuery(id+"F7.opExtrude","SWEPT_FACE",FACE,{"disambiguationData":[OSD([sQuery(id+"F6.wireOp",EDGE,"E20.left")])]})]}),makeQuery(id+"F9.opExtrude","SWEPT_FACE",FACE,{"disambiguationData":[OSD([sQuery(id+"F8.wireOp",EDGE,"E29.right")])]})]})]});
            var Q13;
            Q13=makeQuery(id+"F11.opFillet","BLEND_EDGE",EDGE,{"blendedFrom":[makeQuery(id+"F9.opExtrude","CAP_EDGE",EDGE,{"disambiguationData":[OSD([sQuery(id+"F8.wireOp",EDGE,"E29.bottom")])],"isStart":false}),makeQuery(id+"F9.boolean.opBoolean","MERGE",FACE,{"derivedFrom":[makeQuery(id+"F7.boolean.opBoolean","MERGE",FACE,{"derivedFrom":[makeQuery(id+"F5.boolean.opBoolean","MERGE",FACE,{"derivedFrom":[makeQuery(id+"F3.opExtrude","SWEPT_FACE",FACE,{"disambiguationData":[OSD([sQuery(id+"F2.wireOp",EDGE,"E4.left")])]}),makeQuery(id+"F5.opExtrude","SWEPT_FACE",FACE,{"disambiguationData":[OSD([sQuery(id+"F4.wireOp",EDGE,"E12.left")])]})]}),makeQuery(id+"F7.opExtrude","SWEPT_FACE",FACE,{"disambiguationData":[OSD([sQuery(id+"F6.wireOp",EDGE,"E20.left")])]})]}),makeQuery(id+"F9.opExtrude","SWEPT_FACE",FACE,{"disambiguationData":[OSD([sQuery(id+"F8.wireOp",EDGE,"E29.right")])]})]})],"blendedInto":[makeQuery(id+"F9.boolean.opBoolean","MERGE",FACE,{"derivedFrom":[makeQuery(id+"F7.boolean.opBoolean","MERGE",FACE,{"derivedFrom":[makeQuery(id+"F5.boolean.opBoolean","MERGE",FACE,{"derivedFrom":[makeQuery(id+"F3.opExtrude","SWEPT_FACE",FACE,{"disambiguationData":[OSD([sQuery(id+"F2.wireOp",EDGE,"E4.left")])]}),makeQuery(id+"F5.opExtrude","SWEPT_FACE",FACE,{"disambiguationData":[OSD([sQuery(id+"F4.wireOp",EDGE,"E12.left")])]})]}),makeQuery(id+"F7.opExtrude","SWEPT_FACE",FACE,{"disambiguationData":[OSD([sQuery(id+"F6.wireOp",EDGE,"E20.left")])]})]}),makeQuery(id+"F9.opExtrude","SWEPT_FACE",FACE,{"disambiguationData":[OSD([sQuery(id+"F8.wireOp",EDGE,"E29.right")])]})]})]});
            var Q14;
            Q14=makeQuery(id+"F11.opFillet","BLEND_EDGE",EDGE,{"blendedFrom":[makeQuery(id+"F5.opExtrude","CAP_EDGE",EDGE,{"disambiguationData":[OSD([sQuery(id+"F4.wireOp",EDGE,"E12.bottom")])],"isStart":false}),makeQuery(id+"F9.boolean.opBoolean","MERGE",FACE,{"derivedFrom":[makeQuery(id+"F7.boolean.opBoolean","MERGE",FACE,{"derivedFrom":[makeQuery(id+"F5.boolean.opBoolean","MERGE",FACE,{"derivedFrom":[makeQuery(id+"F3.opExtrude","SWEPT_FACE",FACE,{"disambiguationData":[OSD([sQuery(id+"F2.wireOp",EDGE,"E4.right")])]}),makeQuery(id+"F5.opExtrude","SWEPT_FACE",FACE,{"disambiguationData":[OSD([sQuery(id+"F4.wireOp",EDGE,"E12.right")])]})]}),makeQuery(id+"F7.opExtrude","SWEPT_FACE",FACE,{"disambiguationData":[OSD([sQuery(id+"F6.wireOp",EDGE,"E20.right")])]})]}),makeQuery(id+"F9.opExtrude","SWEPT_FACE",FACE,{"disambiguationData":[OSD([sQuery(id+"F8.wireOp",EDGE,"E29.left")])]})]})],"blendedInto":[makeQuery(id+"F9.boolean.opBoolean","MERGE",FACE,{"derivedFrom":[makeQuery(id+"F7.boolean.opBoolean","MERGE",FACE,{"derivedFrom":[makeQuery(id+"F5.boolean.opBoolean","MERGE",FACE,{"derivedFrom":[makeQuery(id+"F3.opExtrude","SWEPT_FACE",FACE,{"disambiguationData":[OSD([sQuery(id+"F2.wireOp",EDGE,"E4.right")])]}),makeQuery(id+"F5.opExtrude","SWEPT_FACE",FACE,{"disambiguationData":[OSD([sQuery(id+"F4.wireOp",EDGE,"E12.right")])]})]}),makeQuery(id+"F7.opExtrude","SWEPT_FACE",FACE,{"disambiguationData":[OSD([sQuery(id+"F6.wireOp",EDGE,"E20.right")])]})]}),makeQuery(id+"F9.opExtrude","SWEPT_FACE",FACE,{"disambiguationData":[OSD([sQuery(id+"F8.wireOp",EDGE,"E29.left")])]})]})]});
            var Q15;
            Q15=makeQuery(id+"F11.opFillet","BLEND_EDGE",EDGE,{"blendedFrom":[makeQuery(id+"F9.opExtrude","CAP_EDGE",EDGE,{"disambiguationData":[OSD([sQuery(id+"F8.wireOp",EDGE,"E29.bottom")])],"isStart":false}),makeQuery(id+"F9.boolean.opBoolean","MERGE",FACE,{"derivedFrom":[makeQuery(id+"F7.boolean.opBoolean","MERGE",FACE,{"derivedFrom":[makeQuery(id+"F5.boolean.opBoolean","MERGE",FACE,{"derivedFrom":[makeQuery(id+"F3.opExtrude","SWEPT_FACE",FACE,{"disambiguationData":[OSD([sQuery(id+"F2.wireOp",EDGE,"E4.right")])]}),makeQuery(id+"F5.opExtrude","SWEPT_FACE",FACE,{"disambiguationData":[OSD([sQuery(id+"F4.wireOp",EDGE,"E12.right")])]})]}),makeQuery(id+"F7.opExtrude","SWEPT_FACE",FACE,{"disambiguationData":[OSD([sQuery(id+"F6.wireOp",EDGE,"E20.right")])]})]}),makeQuery(id+"F9.opExtrude","SWEPT_FACE",FACE,{"disambiguationData":[OSD([sQuery(id+"F8.wireOp",EDGE,"E29.left")])]})]})],"blendedInto":[makeQuery(id+"F9.boolean.opBoolean","MERGE",FACE,{"derivedFrom":[makeQuery(id+"F7.boolean.opBoolean","MERGE",FACE,{"derivedFrom":[makeQuery(id+"F5.boolean.opBoolean","MERGE",FACE,{"derivedFrom":[makeQuery(id+"F3.opExtrude","SWEPT_FACE",FACE,{"disambiguationData":[OSD([sQuery(id+"F2.wireOp",EDGE,"E4.right")])]}),makeQuery(id+"F5.opExtrude","SWEPT_FACE",FACE,{"disambiguationData":[OSD([sQuery(id+"F4.wireOp",EDGE,"E12.right")])]})]}),makeQuery(id+"F7.opExtrude","SWEPT_FACE",FACE,{"disambiguationData":[OSD([sQuery(id+"F6.wireOp",EDGE,"E20.right")])]})]}),makeQuery(id+"F9.opExtrude","SWEPT_FACE",FACE,{"disambiguationData":[OSD([sQuery(id+"F8.wireOp",EDGE,"E29.left")])]})]})]});
            var Q16;
            Q16=makeQuery(id+"F11.opFillet","BLEND_EDGE",EDGE,{"blendedFrom":[makeQuery(id+"F5.opExtrude","CAP_EDGE",EDGE,{"disambiguationData":[OSD([sQuery(id+"F4.wireOp",EDGE,"E13.bottom")])],"isStart":false}),makeQuery(id+"F9.boolean.opBoolean","MERGE",FACE,{"derivedFrom":[makeQuery(id+"F7.boolean.opBoolean","MERGE",FACE,{"derivedFrom":[makeQuery(id+"F5.boolean.opBoolean","MERGE",FACE,{"derivedFrom":[makeQuery(id+"F3.opExtrude","SWEPT_FACE",FACE,{"disambiguationData":[OSD([sQuery(id+"F2.wireOp",EDGE,"E5.left")])]}),makeQuery(id+"F5.opExtrude","SWEPT_FACE",FACE,{"disambiguationData":[OSD([sQuery(id+"F4.wireOp",EDGE,"E13.left")])]})]}),makeQuery(id+"F7.opExtrude","SWEPT_FACE",FACE,{"disambiguationData":[OSD([sQuery(id+"F6.wireOp",EDGE,"E21.left")])]})]}),makeQuery(id+"F9.opExtrude","SWEPT_FACE",FACE,{"disambiguationData":[OSD([sQuery(id+"F8.wireOp",EDGE,"E28.right")])]})]})],"blendedInto":[makeQuery(id+"F9.boolean.opBoolean","MERGE",FACE,{"derivedFrom":[makeQuery(id+"F7.boolean.opBoolean","MERGE",FACE,{"derivedFrom":[makeQuery(id+"F5.boolean.opBoolean","MERGE",FACE,{"derivedFrom":[makeQuery(id+"F3.opExtrude","SWEPT_FACE",FACE,{"disambiguationData":[OSD([sQuery(id+"F2.wireOp",EDGE,"E5.left")])]}),makeQuery(id+"F5.opExtrude","SWEPT_FACE",FACE,{"disambiguationData":[OSD([sQuery(id+"F4.wireOp",EDGE,"E13.left")])]})]}),makeQuery(id+"F7.opExtrude","SWEPT_FACE",FACE,{"disambiguationData":[OSD([sQuery(id+"F6.wireOp",EDGE,"E21.left")])]})]}),makeQuery(id+"F9.opExtrude","SWEPT_FACE",FACE,{"disambiguationData":[OSD([sQuery(id+"F8.wireOp",EDGE,"E28.right")])]})]})]});
            var Q17;
            Q17=makeQuery(id+"F11.opFillet","BLEND_EDGE",EDGE,{"blendedFrom":[makeQuery(id+"F9.opExtrude","CAP_EDGE",EDGE,{"disambiguationData":[OSD([sQuery(id+"F8.wireOp",EDGE,"E28.bottom")])],"isStart":false}),makeQuery(id+"F9.boolean.opBoolean","MERGE",FACE,{"derivedFrom":[makeQuery(id+"F7.boolean.opBoolean","MERGE",FACE,{"derivedFrom":[makeQuery(id+"F5.boolean.opBoolean","MERGE",FACE,{"derivedFrom":[makeQuery(id+"F3.opExtrude","SWEPT_FACE",FACE,{"disambiguationData":[OSD([sQuery(id+"F2.wireOp",EDGE,"E5.left")])]}),makeQuery(id+"F5.opExtrude","SWEPT_FACE",FACE,{"disambiguationData":[OSD([sQuery(id+"F4.wireOp",EDGE,"E13.left")])]})]}),makeQuery(id+"F7.opExtrude","SWEPT_FACE",FACE,{"disambiguationData":[OSD([sQuery(id+"F6.wireOp",EDGE,"E21.left")])]})]}),makeQuery(id+"F9.opExtrude","SWEPT_FACE",FACE,{"disambiguationData":[OSD([sQuery(id+"F8.wireOp",EDGE,"E28.right")])]})]})],"blendedInto":[makeQuery(id+"F9.boolean.opBoolean","MERGE",FACE,{"derivedFrom":[makeQuery(id+"F7.boolean.opBoolean","MERGE",FACE,{"derivedFrom":[makeQuery(id+"F5.boolean.opBoolean","MERGE",FACE,{"derivedFrom":[makeQuery(id+"F3.opExtrude","SWEPT_FACE",FACE,{"disambiguationData":[OSD([sQuery(id+"F2.wireOp",EDGE,"E5.left")])]}),makeQuery(id+"F5.opExtrude","SWEPT_FACE",FACE,{"disambiguationData":[OSD([sQuery(id+"F4.wireOp",EDGE,"E13.left")])]})]}),makeQuery(id+"F7.opExtrude","SWEPT_FACE",FACE,{"disambiguationData":[OSD([sQuery(id+"F6.wireOp",EDGE,"E21.left")])]})]}),makeQuery(id+"F9.opExtrude","SWEPT_FACE",FACE,{"disambiguationData":[OSD([sQuery(id+"F8.wireOp",EDGE,"E28.right")])]})]})]});
            var Q18;
            Q18=makeQuery(id+"F11.opFillet","BLEND_EDGE",EDGE,{"blendedFrom":[makeQuery(id+"F5.opExtrude","CAP_EDGE",EDGE,{"disambiguationData":[OSD([sQuery(id+"F4.wireOp",EDGE,"E13.bottom")])],"isStart":false}),makeQuery(id+"F9.boolean.opBoolean","MERGE",FACE,{"derivedFrom":[makeQuery(id+"F7.boolean.opBoolean","MERGE",FACE,{"derivedFrom":[makeQuery(id+"F5.boolean.opBoolean","MERGE",FACE,{"derivedFrom":[makeQuery(id+"F3.opExtrude","SWEPT_FACE",FACE,{"disambiguationData":[OSD([sQuery(id+"F2.wireOp",EDGE,"E5.right")])]}),makeQuery(id+"F5.opExtrude","SWEPT_FACE",FACE,{"disambiguationData":[OSD([sQuery(id+"F4.wireOp",EDGE,"E13.right")])]})]}),makeQuery(id+"F7.opExtrude","SWEPT_FACE",FACE,{"disambiguationData":[OSD([sQuery(id+"F6.wireOp",EDGE,"E21.right")])]})]}),makeQuery(id+"F9.opExtrude","SWEPT_FACE",FACE,{"disambiguationData":[OSD([sQuery(id+"F8.wireOp",EDGE,"E28.left")])]})]})],"blendedInto":[makeQuery(id+"F9.boolean.opBoolean","MERGE",FACE,{"derivedFrom":[makeQuery(id+"F7.boolean.opBoolean","MERGE",FACE,{"derivedFrom":[makeQuery(id+"F5.boolean.opBoolean","MERGE",FACE,{"derivedFrom":[makeQuery(id+"F3.opExtrude","SWEPT_FACE",FACE,{"disambiguationData":[OSD([sQuery(id+"F2.wireOp",EDGE,"E5.right")])]}),makeQuery(id+"F5.opExtrude","SWEPT_FACE",FACE,{"disambiguationData":[OSD([sQuery(id+"F4.wireOp",EDGE,"E13.right")])]})]}),makeQuery(id+"F7.opExtrude","SWEPT_FACE",FACE,{"disambiguationData":[OSD([sQuery(id+"F6.wireOp",EDGE,"E21.right")])]})]}),makeQuery(id+"F9.opExtrude","SWEPT_FACE",FACE,{"disambiguationData":[OSD([sQuery(id+"F8.wireOp",EDGE,"E28.left")])]})]})]});
            var Q19;
            Q19=makeQuery(id+"F11.opFillet","BLEND_EDGE",EDGE,{"blendedFrom":[makeQuery(id+"F9.opExtrude","CAP_EDGE",EDGE,{"disambiguationData":[OSD([sQuery(id+"F8.wireOp",EDGE,"E28.bottom")])],"isStart":false}),makeQuery(id+"F9.boolean.opBoolean","MERGE",FACE,{"derivedFrom":[makeQuery(id+"F7.boolean.opBoolean","MERGE",FACE,{"derivedFrom":[makeQuery(id+"F5.boolean.opBoolean","MERGE",FACE,{"derivedFrom":[makeQuery(id+"F3.opExtrude","SWEPT_FACE",FACE,{"disambiguationData":[OSD([sQuery(id+"F2.wireOp",EDGE,"E5.right")])]}),makeQuery(id+"F5.opExtrude","SWEPT_FACE",FACE,{"disambiguationData":[OSD([sQuery(id+"F4.wireOp",EDGE,"E13.right")])]})]}),makeQuery(id+"F7.opExtrude","SWEPT_FACE",FACE,{"disambiguationData":[OSD([sQuery(id+"F6.wireOp",EDGE,"E21.right")])]})]}),makeQuery(id+"F9.opExtrude","SWEPT_FACE",FACE,{"disambiguationData":[OSD([sQuery(id+"F8.wireOp",EDGE,"E28.left")])]})]})],"blendedInto":[makeQuery(id+"F9.boolean.opBoolean","MERGE",FACE,{"derivedFrom":[makeQuery(id+"F7.boolean.opBoolean","MERGE",FACE,{"derivedFrom":[makeQuery(id+"F5.boolean.opBoolean","MERGE",FACE,{"derivedFrom":[makeQuery(id+"F3.opExtrude","SWEPT_FACE",FACE,{"disambiguationData":[OSD([sQuery(id+"F2.wireOp",EDGE,"E5.right")])]}),makeQuery(id+"F5.opExtrude","SWEPT_FACE",FACE,{"disambiguationData":[OSD([sQuery(id+"F4.wireOp",EDGE,"E13.right")])]})]}),makeQuery(id+"F7.opExtrude","SWEPT_FACE",FACE,{"disambiguationData":[OSD([sQuery(id+"F6.wireOp",EDGE,"E21.right")])]})]}),makeQuery(id+"F9.opExtrude","SWEPT_FACE",FACE,{"disambiguationData":[OSD([sQuery(id+"F8.wireOp",EDGE,"E28.left")])]})]})]});
            var Q20;
            Q20=makeQuery(id+"F11.opFillet","BLEND_EDGE",EDGE,{"blendedFrom":[makeQuery(id+"F5.opExtrude","CAP_EDGE",EDGE,{"disambiguationData":[OSD([sQuery(id+"F4.wireOp",EDGE,"E14.bottom")])],"isStart":false}),makeQuery(id+"F9.boolean.opBoolean","MERGE",FACE,{"derivedFrom":[makeQuery(id+"F7.boolean.opBoolean","MERGE",FACE,{"derivedFrom":[makeQuery(id+"F5.boolean.opBoolean","MERGE",FACE,{"derivedFrom":[makeQuery(id+"F3.opExtrude","SWEPT_FACE",FACE,{"disambiguationData":[OSD([sQuery(id+"F2.wireOp",EDGE,"E6.left")])]}),makeQuery(id+"F5.opExtrude","SWEPT_FACE",FACE,{"disambiguationData":[OSD([sQuery(id+"F4.wireOp",EDGE,"E14.left")])]})]}),makeQuery(id+"F7.opExtrude","SWEPT_FACE",FACE,{"disambiguationData":[OSD([sQuery(id+"F6.wireOp",EDGE,"E22.left")])]})]}),makeQuery(id+"F9.opExtrude","SWEPT_FACE",FACE,{"disambiguationData":[OSD([sQuery(id+"F8.wireOp",EDGE,"E27.right")])]})]})],"blendedInto":[makeQuery(id+"F9.boolean.opBoolean","MERGE",FACE,{"derivedFrom":[makeQuery(id+"F7.boolean.opBoolean","MERGE",FACE,{"derivedFrom":[makeQuery(id+"F5.boolean.opBoolean","MERGE",FACE,{"derivedFrom":[makeQuery(id+"F3.opExtrude","SWEPT_FACE",FACE,{"disambiguationData":[OSD([sQuery(id+"F2.wireOp",EDGE,"E6.left")])]}),makeQuery(id+"F5.opExtrude","SWEPT_FACE",FACE,{"disambiguationData":[OSD([sQuery(id+"F4.wireOp",EDGE,"E14.left")])]})]}),makeQuery(id+"F7.opExtrude","SWEPT_FACE",FACE,{"disambiguationData":[OSD([sQuery(id+"F6.wireOp",EDGE,"E22.left")])]})]}),makeQuery(id+"F9.opExtrude","SWEPT_FACE",FACE,{"disambiguationData":[OSD([sQuery(id+"F8.wireOp",EDGE,"E27.right")])]})]})]});
            var Q21;
            Q21=makeQuery(id+"F11.opFillet","BLEND_EDGE",EDGE,{"blendedFrom":[makeQuery(id+"F9.opExtrude","CAP_EDGE",EDGE,{"disambiguationData":[OSD([sQuery(id+"F8.wireOp",EDGE,"E27.bottom")])],"isStart":false}),makeQuery(id+"F9.boolean.opBoolean","MERGE",FACE,{"derivedFrom":[makeQuery(id+"F7.boolean.opBoolean","MERGE",FACE,{"derivedFrom":[makeQuery(id+"F5.boolean.opBoolean","MERGE",FACE,{"derivedFrom":[makeQuery(id+"F3.opExtrude","SWEPT_FACE",FACE,{"disambiguationData":[OSD([sQuery(id+"F2.wireOp",EDGE,"E6.left")])]}),makeQuery(id+"F5.opExtrude","SWEPT_FACE",FACE,{"disambiguationData":[OSD([sQuery(id+"F4.wireOp",EDGE,"E14.left")])]})]}),makeQuery(id+"F7.opExtrude","SWEPT_FACE",FACE,{"disambiguationData":[OSD([sQuery(id+"F6.wireOp",EDGE,"E22.left")])]})]}),makeQuery(id+"F9.opExtrude","SWEPT_FACE",FACE,{"disambiguationData":[OSD([sQuery(id+"F8.wireOp",EDGE,"E27.right")])]})]})],"blendedInto":[makeQuery(id+"F9.boolean.opBoolean","MERGE",FACE,{"derivedFrom":[makeQuery(id+"F7.boolean.opBoolean","MERGE",FACE,{"derivedFrom":[makeQuery(id+"F5.boolean.opBoolean","MERGE",FACE,{"derivedFrom":[makeQuery(id+"F3.opExtrude","SWEPT_FACE",FACE,{"disambiguationData":[OSD([sQuery(id+"F2.wireOp",EDGE,"E6.left")])]}),makeQuery(id+"F5.opExtrude","SWEPT_FACE",FACE,{"disambiguationData":[OSD([sQuery(id+"F4.wireOp",EDGE,"E14.left")])]})]}),makeQuery(id+"F7.opExtrude","SWEPT_FACE",FACE,{"disambiguationData":[OSD([sQuery(id+"F6.wireOp",EDGE,"E22.left")])]})]}),makeQuery(id+"F9.opExtrude","SWEPT_FACE",FACE,{"disambiguationData":[OSD([sQuery(id+"F8.wireOp",EDGE,"E27.right")])]})]})]});
            var Q22;
            Q22=makeQuery(id+"F11.opFillet","BLEND_EDGE",EDGE,{"blendedFrom":[makeQuery(id+"F5.opExtrude","CAP_EDGE",EDGE,{"disambiguationData":[OSD([sQuery(id+"F4.wireOp",EDGE,"E14.bottom")])],"isStart":false}),makeQuery(id+"F9.boolean.opBoolean","MERGE",FACE,{"derivedFrom":[makeQuery(id+"F7.boolean.opBoolean","MERGE",FACE,{"derivedFrom":[makeQuery(id+"F5.boolean.opBoolean","MERGE",FACE,{"derivedFrom":[makeQuery(id+"F3.opExtrude","SWEPT_FACE",FACE,{"disambiguationData":[OSD([sQuery(id+"F2.wireOp",EDGE,"E6.right")])]}),makeQuery(id+"F5.opExtrude","SWEPT_FACE",FACE,{"disambiguationData":[OSD([sQuery(id+"F4.wireOp",EDGE,"E14.right")])]})]}),makeQuery(id+"F7.opExtrude","SWEPT_FACE",FACE,{"disambiguationData":[OSD([sQuery(id+"F6.wireOp",EDGE,"E22.right")])]})]}),makeQuery(id+"F9.opExtrude","SWEPT_FACE",FACE,{"disambiguationData":[OSD([sQuery(id+"F8.wireOp",EDGE,"E27.left")])]})]})],"blendedInto":[makeQuery(id+"F9.boolean.opBoolean","MERGE",FACE,{"derivedFrom":[makeQuery(id+"F7.boolean.opBoolean","MERGE",FACE,{"derivedFrom":[makeQuery(id+"F5.boolean.opBoolean","MERGE",FACE,{"derivedFrom":[makeQuery(id+"F3.opExtrude","SWEPT_FACE",FACE,{"disambiguationData":[OSD([sQuery(id+"F2.wireOp",EDGE,"E6.right")])]}),makeQuery(id+"F5.opExtrude","SWEPT_FACE",FACE,{"disambiguationData":[OSD([sQuery(id+"F4.wireOp",EDGE,"E14.right")])]})]}),makeQuery(id+"F7.opExtrude","SWEPT_FACE",FACE,{"disambiguationData":[OSD([sQuery(id+"F6.wireOp",EDGE,"E22.right")])]})]}),makeQuery(id+"F9.opExtrude","SWEPT_FACE",FACE,{"disambiguationData":[OSD([sQuery(id+"F8.wireOp",EDGE,"E27.left")])]})]})]});
            var Q23;
            Q23=makeQuery(id+"F11.opFillet","BLEND_EDGE",EDGE,{"blendedFrom":[makeQuery(id+"F9.opExtrude","CAP_EDGE",EDGE,{"disambiguationData":[OSD([sQuery(id+"F8.wireOp",EDGE,"E27.bottom")])],"isStart":false}),makeQuery(id+"F9.boolean.opBoolean","MERGE",FACE,{"derivedFrom":[makeQuery(id+"F7.boolean.opBoolean","MERGE",FACE,{"derivedFrom":[makeQuery(id+"F5.boolean.opBoolean","MERGE",FACE,{"derivedFrom":[makeQuery(id+"F3.opExtrude","SWEPT_FACE",FACE,{"disambiguationData":[OSD([sQuery(id+"F2.wireOp",EDGE,"E6.right")])]}),makeQuery(id+"F5.opExtrude","SWEPT_FACE",FACE,{"disambiguationData":[OSD([sQuery(id+"F4.wireOp",EDGE,"E14.right")])]})]}),makeQuery(id+"F7.opExtrude","SWEPT_FACE",FACE,{"disambiguationData":[OSD([sQuery(id+"F6.wireOp",EDGE,"E22.right")])]})]}),makeQuery(id+"F9.opExtrude","SWEPT_FACE",FACE,{"disambiguationData":[OSD([sQuery(id+"F8.wireOp",EDGE,"E27.left")])]})]})],"blendedInto":[makeQuery(id+"F9.boolean.opBoolean","MERGE",FACE,{"derivedFrom":[makeQuery(id+"F7.boolean.opBoolean","MERGE",FACE,{"derivedFrom":[makeQuery(id+"F5.boolean.opBoolean","MERGE",FACE,{"derivedFrom":[makeQuery(id+"F3.opExtrude","SWEPT_FACE",FACE,{"disambiguationData":[OSD([sQuery(id+"F2.wireOp",EDGE,"E6.right")])]}),makeQuery(id+"F5.opExtrude","SWEPT_FACE",FACE,{"disambiguationData":[OSD([sQuery(id+"F4.wireOp",EDGE,"E14.right")])]})]}),makeQuery(id+"F7.opExtrude","SWEPT_FACE",FACE,{"disambiguationData":[OSD([sQuery(id+"F6.wireOp",EDGE,"E22.right")])]})]}),makeQuery(id+"F9.opExtrude","SWEPT_FACE",FACE,{"disambiguationData":[OSD([sQuery(id+"F8.wireOp",EDGE,"E27.left")])]})]})]});
            var Q24;
            Q24=makeQuery(id+"F11.opFillet","BLEND_EDGE",EDGE,{"blendedFrom":[makeQuery(id+"F5.opExtrude","CAP_EDGE",EDGE,{"disambiguationData":[OSD([sQuery(id+"F4.wireOp",EDGE,"E15.bottom")])],"isStart":false}),makeQuery(id+"F9.boolean.opBoolean","MERGE",FACE,{"derivedFrom":[makeQuery(id+"F7.boolean.opBoolean","MERGE",FACE,{"derivedFrom":[makeQuery(id+"F5.boolean.opBoolean","MERGE",FACE,{"derivedFrom":[makeQuery(id+"F3.opExtrude","SWEPT_FACE",FACE,{"disambiguationData":[OSD([sQuery(id+"F2.wireOp",EDGE,"E7.left")])]}),makeQuery(id+"F5.opExtrude","SWEPT_FACE",FACE,{"disambiguationData":[OSD([sQuery(id+"F4.wireOp",EDGE,"E15.left")])]})]}),makeQuery(id+"F7.opExtrude","SWEPT_FACE",FACE,{"disambiguationData":[OSD([sQuery(id+"F6.wireOp",EDGE,"E23.left")])]})]}),makeQuery(id+"F9.opExtrude","SWEPT_FACE",FACE,{"disambiguationData":[OSD([sQuery(id+"F8.wireOp",EDGE,"E26.right")])]})]})],"blendedInto":[makeQuery(id+"F9.boolean.opBoolean","MERGE",FACE,{"derivedFrom":[makeQuery(id+"F7.boolean.opBoolean","MERGE",FACE,{"derivedFrom":[makeQuery(id+"F5.boolean.opBoolean","MERGE",FACE,{"derivedFrom":[makeQuery(id+"F3.opExtrude","SWEPT_FACE",FACE,{"disambiguationData":[OSD([sQuery(id+"F2.wireOp",EDGE,"E7.left")])]}),makeQuery(id+"F5.opExtrude","SWEPT_FACE",FACE,{"disambiguationData":[OSD([sQuery(id+"F4.wireOp",EDGE,"E15.left")])]})]}),makeQuery(id+"F7.opExtrude","SWEPT_FACE",FACE,{"disambiguationData":[OSD([sQuery(id+"F6.wireOp",EDGE,"E23.left")])]})]}),makeQuery(id+"F9.opExtrude","SWEPT_FACE",FACE,{"disambiguationData":[OSD([sQuery(id+"F8.wireOp",EDGE,"E26.right")])]})]})]});
            var Q25;
            Q25=makeQuery(id+"F11.opFillet","BLEND_EDGE",EDGE,{"blendedFrom":[makeQuery(id+"F9.opExtrude","CAP_EDGE",EDGE,{"disambiguationData":[OSD([sQuery(id+"F8.wireOp",EDGE,"E26.bottom")])],"isStart":false}),makeQuery(id+"F9.boolean.opBoolean","MERGE",FACE,{"derivedFrom":[makeQuery(id+"F7.boolean.opBoolean","MERGE",FACE,{"derivedFrom":[makeQuery(id+"F5.boolean.opBoolean","MERGE",FACE,{"derivedFrom":[makeQuery(id+"F3.opExtrude","SWEPT_FACE",FACE,{"disambiguationData":[OSD([sQuery(id+"F2.wireOp",EDGE,"E7.left")])]}),makeQuery(id+"F5.opExtrude","SWEPT_FACE",FACE,{"disambiguationData":[OSD([sQuery(id+"F4.wireOp",EDGE,"E15.left")])]})]}),makeQuery(id+"F7.opExtrude","SWEPT_FACE",FACE,{"disambiguationData":[OSD([sQuery(id+"F6.wireOp",EDGE,"E23.left")])]})]}),makeQuery(id+"F9.opExtrude","SWEPT_FACE",FACE,{"disambiguationData":[OSD([sQuery(id+"F8.wireOp",EDGE,"E26.right")])]})]})],"blendedInto":[makeQuery(id+"F9.boolean.opBoolean","MERGE",FACE,{"derivedFrom":[makeQuery(id+"F7.boolean.opBoolean","MERGE",FACE,{"derivedFrom":[makeQuery(id+"F5.boolean.opBoolean","MERGE",FACE,{"derivedFrom":[makeQuery(id+"F3.opExtrude","SWEPT_FACE",FACE,{"disambiguationData":[OSD([sQuery(id+"F2.wireOp",EDGE,"E7.left")])]}),makeQuery(id+"F5.opExtrude","SWEPT_FACE",FACE,{"disambiguationData":[OSD([sQuery(id+"F4.wireOp",EDGE,"E15.left")])]})]}),makeQuery(id+"F7.opExtrude","SWEPT_FACE",FACE,{"disambiguationData":[OSD([sQuery(id+"F6.wireOp",EDGE,"E23.left")])]})]}),makeQuery(id+"F9.opExtrude","SWEPT_FACE",FACE,{"disambiguationData":[OSD([sQuery(id+"F8.wireOp",EDGE,"E26.right")])]})]})]});
            var Q26;
            Q26=makeQuery(id+"F11.opFillet","BLEND_EDGE",EDGE,{"blendedFrom":[makeQuery(id+"F5.opExtrude","CAP_EDGE",EDGE,{"disambiguationData":[OSD([sQuery(id+"F4.wireOp",EDGE,"E15.bottom")])],"isStart":false}),makeQuery(id+"F9.boolean.opBoolean","MERGE",FACE,{"derivedFrom":[makeQuery(id+"F7.boolean.opBoolean","MERGE",FACE,{"derivedFrom":[makeQuery(id+"F5.boolean.opBoolean","MERGE",FACE,{"derivedFrom":[makeQuery(id+"F3.opExtrude","SWEPT_FACE",FACE,{"disambiguationData":[OSD([sQuery(id+"F2.wireOp",EDGE,"E7.right")])]}),makeQuery(id+"F5.opExtrude","SWEPT_FACE",FACE,{"disambiguationData":[OSD([sQuery(id+"F4.wireOp",EDGE,"E15.right")])]})]}),makeQuery(id+"F7.opExtrude","SWEPT_FACE",FACE,{"disambiguationData":[OSD([sQuery(id+"F6.wireOp",EDGE,"E23.right")])]})]}),makeQuery(id+"F9.opExtrude","SWEPT_FACE",FACE,{"disambiguationData":[OSD([sQuery(id+"F8.wireOp",EDGE,"E26.left")])]})]})],"blendedInto":[makeQuery(id+"F9.boolean.opBoolean","MERGE",FACE,{"derivedFrom":[makeQuery(id+"F7.boolean.opBoolean","MERGE",FACE,{"derivedFrom":[makeQuery(id+"F5.boolean.opBoolean","MERGE",FACE,{"derivedFrom":[makeQuery(id+"F3.opExtrude","SWEPT_FACE",FACE,{"disambiguationData":[OSD([sQuery(id+"F2.wireOp",EDGE,"E7.right")])]}),makeQuery(id+"F5.opExtrude","SWEPT_FACE",FACE,{"disambiguationData":[OSD([sQuery(id+"F4.wireOp",EDGE,"E15.right")])]})]}),makeQuery(id+"F7.opExtrude","SWEPT_FACE",FACE,{"disambiguationData":[OSD([sQuery(id+"F6.wireOp",EDGE,"E23.right")])]})]}),makeQuery(id+"F9.opExtrude","SWEPT_FACE",FACE,{"disambiguationData":[OSD([sQuery(id+"F8.wireOp",EDGE,"E26.left")])]})]})]});
            var Q27;
            Q27=makeQuery(id+"F11.opFillet","BLEND_EDGE",EDGE,{"blendedFrom":[makeQuery(id+"F9.opExtrude","CAP_EDGE",EDGE,{"disambiguationData":[OSD([sQuery(id+"F8.wireOp",EDGE,"E26.bottom")])],"isStart":false}),makeQuery(id+"F9.boolean.opBoolean","MERGE",FACE,{"derivedFrom":[makeQuery(id+"F7.boolean.opBoolean","MERGE",FACE,{"derivedFrom":[makeQuery(id+"F5.boolean.opBoolean","MERGE",FACE,{"derivedFrom":[makeQuery(id+"F3.opExtrude","SWEPT_FACE",FACE,{"disambiguationData":[OSD([sQuery(id+"F2.wireOp",EDGE,"E7.right")])]}),makeQuery(id+"F5.opExtrude","SWEPT_FACE",FACE,{"disambiguationData":[OSD([sQuery(id+"F4.wireOp",EDGE,"E15.right")])]})]}),makeQuery(id+"F7.opExtrude","SWEPT_FACE",FACE,{"disambiguationData":[OSD([sQuery(id+"F6.wireOp",EDGE,"E23.right")])]})]}),makeQuery(id+"F9.opExtrude","SWEPT_FACE",FACE,{"disambiguationData":[OSD([sQuery(id+"F8.wireOp",EDGE,"E26.left")])]})]})],"blendedInto":[makeQuery(id+"F9.boolean.opBoolean","MERGE",FACE,{"derivedFrom":[makeQuery(id+"F7.boolean.opBoolean","MERGE",FACE,{"derivedFrom":[makeQuery(id+"F5.boolean.opBoolean","MERGE",FACE,{"derivedFrom":[makeQuery(id+"F3.opExtrude","SWEPT_FACE",FACE,{"disambiguationData":[OSD([sQuery(id+"F2.wireOp",EDGE,"E7.right")])]}),makeQuery(id+"F5.opExtrude","SWEPT_FACE",FACE,{"disambiguationData":[OSD([sQuery(id+"F4.wireOp",EDGE,"E15.right")])]})]}),makeQuery(id+"F7.opExtrude","SWEPT_FACE",FACE,{"disambiguationData":[OSD([sQuery(id+"F6.wireOp",EDGE,"E23.right")])]})]}),makeQuery(id+"F9.opExtrude","SWEPT_FACE",FACE,{"disambiguationData":[OSD([sQuery(id+"F8.wireOp",EDGE,"E26.left")])]})]})]});
            var Q28;
            Q28=makeQuery(id+"F11.opFillet","BLEND_EDGE",EDGE,{"blendedFrom":[makeQuery(id+"F5.opExtrude","CAP_EDGE",EDGE,{"disambiguationData":[OSD([sQuery(id+"F4.wireOp",EDGE,"E16.bottom")])],"isStart":false}),makeQuery(id+"F9.boolean.opBoolean","MERGE",FACE,{"derivedFrom":[makeQuery(id+"F7.boolean.opBoolean","MERGE",FACE,{"derivedFrom":[makeQuery(id+"F5.boolean.opBoolean","MERGE",FACE,{"derivedFrom":[makeQuery(id+"F3.opExtrude","SWEPT_FACE",FACE,{"disambiguationData":[OSD([sQuery(id+"F2.wireOp",EDGE,"E8.left")])]}),makeQuery(id+"F5.opExtrude","SWEPT_FACE",FACE,{"disambiguationData":[OSD([sQuery(id+"F4.wireOp",EDGE,"E16.left")])]})]}),makeQuery(id+"F7.opExtrude","SWEPT_FACE",FACE,{"disambiguationData":[OSD([sQuery(id+"F6.wireOp",EDGE,"E24.left")])]})]}),makeQuery(id+"F9.opExtrude","SWEPT_FACE",FACE,{"disambiguationData":[OSD([sQuery(id+"F8.wireOp",EDGE,"E25.right")])]})]})],"blendedInto":[makeQuery(id+"F9.boolean.opBoolean","MERGE",FACE,{"derivedFrom":[makeQuery(id+"F7.boolean.opBoolean","MERGE",FACE,{"derivedFrom":[makeQuery(id+"F5.boolean.opBoolean","MERGE",FACE,{"derivedFrom":[makeQuery(id+"F3.opExtrude","SWEPT_FACE",FACE,{"disambiguationData":[OSD([sQuery(id+"F2.wireOp",EDGE,"E8.left")])]}),makeQuery(id+"F5.opExtrude","SWEPT_FACE",FACE,{"disambiguationData":[OSD([sQuery(id+"F4.wireOp",EDGE,"E16.left")])]})]}),makeQuery(id+"F7.opExtrude","SWEPT_FACE",FACE,{"disambiguationData":[OSD([sQuery(id+"F6.wireOp",EDGE,"E24.left")])]})]}),makeQuery(id+"F9.opExtrude","SWEPT_FACE",FACE,{"disambiguationData":[OSD([sQuery(id+"F8.wireOp",EDGE,"E25.right")])]})]})]});
            var Q29;
            Q29=makeQuery(id+"F11.opFillet","BLEND_EDGE",EDGE,{"blendedFrom":[makeQuery(id+"F9.opExtrude","CAP_EDGE",EDGE,{"disambiguationData":[OSD([sQuery(id+"F8.wireOp",EDGE,"E25.bottom")])],"isStart":false}),makeQuery(id+"F9.boolean.opBoolean","MERGE",FACE,{"derivedFrom":[makeQuery(id+"F7.boolean.opBoolean","MERGE",FACE,{"derivedFrom":[makeQuery(id+"F5.boolean.opBoolean","MERGE",FACE,{"derivedFrom":[makeQuery(id+"F3.opExtrude","SWEPT_FACE",FACE,{"disambiguationData":[OSD([sQuery(id+"F2.wireOp",EDGE,"E8.left")])]}),makeQuery(id+"F5.opExtrude","SWEPT_FACE",FACE,{"disambiguationData":[OSD([sQuery(id+"F4.wireOp",EDGE,"E16.left")])]})]}),makeQuery(id+"F7.opExtrude","SWEPT_FACE",FACE,{"disambiguationData":[OSD([sQuery(id+"F6.wireOp",EDGE,"E24.left")])]})]}),makeQuery(id+"F9.opExtrude","SWEPT_FACE",FACE,{"disambiguationData":[OSD([sQuery(id+"F8.wireOp",EDGE,"E25.right")])]})]})],"blendedInto":[makeQuery(id+"F9.boolean.opBoolean","MERGE",FACE,{"derivedFrom":[makeQuery(id+"F7.boolean.opBoolean","MERGE",FACE,{"derivedFrom":[makeQuery(id+"F5.boolean.opBoolean","MERGE",FACE,{"derivedFrom":[makeQuery(id+"F3.opExtrude","SWEPT_FACE",FACE,{"disambiguationData":[OSD([sQuery(id+"F2.wireOp",EDGE,"E8.left")])]}),makeQuery(id+"F5.opExtrude","SWEPT_FACE",FACE,{"disambiguationData":[OSD([sQuery(id+"F4.wireOp",EDGE,"E16.left")])]})]}),makeQuery(id+"F7.opExtrude","SWEPT_FACE",FACE,{"disambiguationData":[OSD([sQuery(id+"F6.wireOp",EDGE,"E24.left")])]})]}),makeQuery(id+"F9.opExtrude","SWEPT_FACE",FACE,{"disambiguationData":[OSD([sQuery(id+"F8.wireOp",EDGE,"E25.right")])]})]})]});
            var Q30;
            Q30=makeQuery(id+"F11.opFillet","BLEND_EDGE",EDGE,{"blendedFrom":[makeQuery(id+"F9.opExtrude","CAP_EDGE",EDGE,{"disambiguationData":[OSD([sQuery(id+"F8.wireOp",EDGE,"E25.bottom")])],"isStart":false}),makeQuery(id+"F9.boolean.opBoolean","MERGE",FACE,{"derivedFrom":[makeQuery(id+"F7.boolean.opBoolean","MERGE",FACE,{"derivedFrom":[makeQuery(id+"F5.boolean.opBoolean","MERGE",FACE,{"derivedFrom":[makeQuery(id+"F3.boolean.opBoolean","MERGE",FACE,{"derivedFrom":[makeQuery(id+"F1.opExtrude","SWEPT_FACE",FACE,{"disambiguationData":[OSD([sQuery(id+"F0.wireOp",EDGE,"E0.right")])]}),makeQuery(id+"F3.opExtrude","SWEPT_FACE",FACE,{"disambiguationData":[OSD([sQuery(id+"F2.wireOp",EDGE,"E8.right")])]})]}),makeQuery(id+"F5.opExtrude","SWEPT_FACE",FACE,{"disambiguationData":[OSD([sQuery(id+"F4.wireOp",EDGE,"E16.right")])]})]}),makeQuery(id+"F7.opExtrude","SWEPT_FACE",FACE,{"disambiguationData":[OSD([sQuery(id+"F6.wireOp",EDGE,"E24.right")])]})]}),makeQuery(id+"F9.opExtrude","SWEPT_FACE",FACE,{"disambiguationData":[OSD([sQuery(id+"F8.wireOp",EDGE,"E25.left")])]})]})],"blendedInto":[makeQuery(id+"F9.boolean.opBoolean","MERGE",FACE,{"derivedFrom":[makeQuery(id+"F7.boolean.opBoolean","MERGE",FACE,{"derivedFrom":[makeQuery(id+"F5.boolean.opBoolean","MERGE",FACE,{"derivedFrom":[makeQuery(id+"F3.boolean.opBoolean","MERGE",FACE,{"derivedFrom":[makeQuery(id+"F1.opExtrude","SWEPT_FACE",FACE,{"disambiguationData":[OSD([sQuery(id+"F0.wireOp",EDGE,"E0.right")])]}),makeQuery(id+"F3.opExtrude","SWEPT_FACE",FACE,{"disambiguationData":[OSD([sQuery(id+"F2.wireOp",EDGE,"E8.right")])]})]}),makeQuery(id+"F5.opExtrude","SWEPT_FACE",FACE,{"disambiguationData":[OSD([sQuery(id+"F4.wireOp",EDGE,"E16.right")])]})]}),makeQuery(id+"F7.opExtrude","SWEPT_FACE",FACE,{"disambiguationData":[OSD([sQuery(id+"F6.wireOp",EDGE,"E24.right")])]})]}),makeQuery(id+"F9.opExtrude","SWEPT_FACE",FACE,{"disambiguationData":[OSD([sQuery(id+"F8.wireOp",EDGE,"E25.left")])]})]})]});
            var Q31;
            Q31=makeQuery(id+"F11.opFillet","BLEND_EDGE",EDGE,{"blendedFrom":[makeQuery(id+"F5.opExtrude","CAP_EDGE",EDGE,{"disambiguationData":[OSD([sQuery(id+"F4.wireOp",EDGE,"E16.bottom")])],"isStart":false}),makeQuery(id+"F9.boolean.opBoolean","MERGE",FACE,{"derivedFrom":[makeQuery(id+"F7.boolean.opBoolean","MERGE",FACE,{"derivedFrom":[makeQuery(id+"F5.boolean.opBoolean","MERGE",FACE,{"derivedFrom":[makeQuery(id+"F3.boolean.opBoolean","MERGE",FACE,{"derivedFrom":[makeQuery(id+"F1.opExtrude","SWEPT_FACE",FACE,{"disambiguationData":[OSD([sQuery(id+"F0.wireOp",EDGE,"E0.right")])]}),makeQuery(id+"F3.opExtrude","SWEPT_FACE",FACE,{"disambiguationData":[OSD([sQuery(id+"F2.wireOp",EDGE,"E8.right")])]})]}),makeQuery(id+"F5.opExtrude","SWEPT_FACE",FACE,{"disambiguationData":[OSD([sQuery(id+"F4.wireOp",EDGE,"E16.right")])]})]}),makeQuery(id+"F7.opExtrude","SWEPT_FACE",FACE,{"disambiguationData":[OSD([sQuery(id+"F6.wireOp",EDGE,"E24.right")])]})]}),makeQuery(id+"F9.opExtrude","SWEPT_FACE",FACE,{"disambiguationData":[OSD([sQuery(id+"F8.wireOp",EDGE,"E25.left")])]})]})],"blendedInto":[makeQuery(id+"F9.boolean.opBoolean","MERGE",FACE,{"derivedFrom":[makeQuery(id+"F7.boolean.opBoolean","MERGE",FACE,{"derivedFrom":[makeQuery(id+"F5.boolean.opBoolean","MERGE",FACE,{"derivedFrom":[makeQuery(id+"F3.boolean.opBoolean","MERGE",FACE,{"derivedFrom":[makeQuery(id+"F1.opExtrude","SWEPT_FACE",FACE,{"disambiguationData":[OSD([sQuery(id+"F0.wireOp",EDGE,"E0.right")])]}),makeQuery(id+"F3.opExtrude","SWEPT_FACE",FACE,{"disambiguationData":[OSD([sQuery(id+"F2.wireOp",EDGE,"E8.right")])]})]}),makeQuery(id+"F5.opExtrude","SWEPT_FACE",FACE,{"disambiguationData":[OSD([sQuery(id+"F4.wireOp",EDGE,"E16.right")])]})]}),makeQuery(id+"F7.opExtrude","SWEPT_FACE",FACE,{"disambiguationData":[OSD([sQuery(id+"F6.wireOp",EDGE,"E24.right")])]})]}),makeQuery(id+"F9.opExtrude","SWEPT_FACE",FACE,{"disambiguationData":[OSD([sQuery(id+"F8.wireOp",EDGE,"E25.left")])]})]})]});
            fillet(context, id + "F12", {"entities" : qUnion([Q0, Q1, Q2, Q3, Q4, Q5, Q6, Q7, Q8, Q9, Q10, Q11, Q12, Q13, Q14, Q15, Q16, Q17, Q18, Q19, Q20, Q21, Q22, Q23, Q24, Q25, Q26, Q27, Q28, Q29, Q30, Q31]), "radius" : 1.27 * mm, "tangentPropagation" : true, "allowEdgeOverflow" : false});
        }
    });
